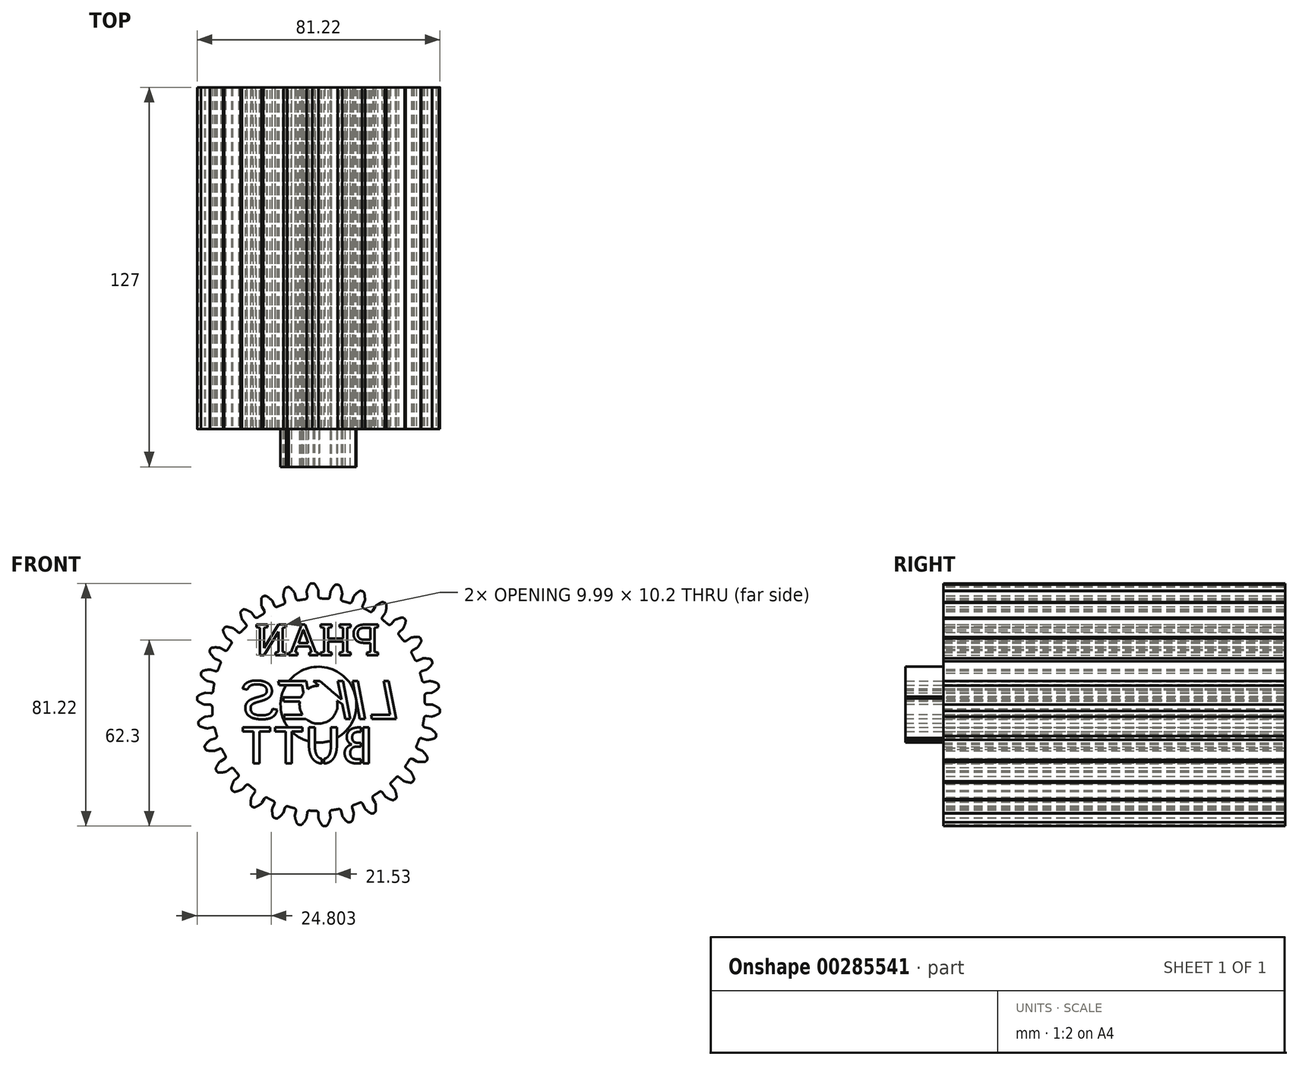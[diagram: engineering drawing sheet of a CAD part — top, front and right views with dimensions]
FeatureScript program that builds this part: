
annotation { "Feature Type Name" : "Feature", "Feature Type Description" : "" }
export const myFeature = defineFeature(function(context is Context, id is Id, definition is map)
    precondition{}
    {
        {
            var Q0;
            Q0=qCreatedBy(makeId("Front.planeOp"),FACE);
            var sketch = newSketch(context, id + "F0", { "sketchPlane" : qUnion([Q0])});
            skCircle(sketch, "E0", {"center": v(0, 0) * mm, "radius": 35.56 * mm});
            skSolve(sketch);
        }
        {
            var Q0;
            Q0=makeQuery(id+"F0.imprint","IMPRINT",FACE,{"disambiguationData":[TD([[makeQuery(id+"F0.imprint","IMPRINT",EDGE,{"derivedFrom":sQuery(id+"F0.wireOp",EDGE,"E0")}),1.0]])]});
            extrude(context, id + "F1", {"entities" : qUnion([Q0]), "depth" : 114.3 * mm});
        }
        {
            var Q0;
            Q0=makeQuery(id+"F1.opExtrude","CAP_FACE",FACE,{"disambiguationData":[OSD([sQuery(id+"F0.wireOp",EDGE,"E0")])],"isStart":false});
            var sketch = newSketch(context, id + "F2", { "sketchPlane" : qUnion([Q0])});
            skArc(sketch, "E1.trimOffspring", {"start": v(-0.06, 38.24) * mm, "mid": v(-0.56, 39.3) * mm, "end": v(-1.2, 40.3) * mm});
            skLineSegment(sketch, "E2", {"start": v(-1.82, 40.61) * mm, "end": v(-2.13, 40.61) * mm});
            skLineSegment(sketch, "E3", {"start": v(0, 37.96) * mm, "end": v(0, 36.31) * mm});
            skLineSegment(sketch, "E4.MirrorCS", {"start": v(-3.97, 37.75) * mm, "end": v(-3.8, 36.12) * mm});
            skArc(sketch, "E5.MirrorCS", {"start": v(-3.94, 38.04) * mm, "mid": v(-3.55, 39.15) * mm, "end": v(-3.02, 40.2) * mm});
            skLineSegment(sketch, "E6.MirrorCS", {"start": v(-2.44, 40.58) * mm, "end": v(-2.13, 40.61) * mm});
            skPoint(sketch, "E7.visualSharp", {"position": v(-3.72, 35.37) * mm});
            skArc(sketch, "E7.filletArc", {"start": v(-4.46, 35.28) * mm, "mid": v(-3.96, 35.56) * mm, "end": v(-3.8, 36.12) * mm});
            skPoint(sketch, "E8.visualSharp", {"position": v(0, 35.56) * mm});
            skArc(sketch, "E8.filletArc", {"start": v(0, 36.31) * mm, "mid": v(0.22, 35.78) * mm, "end": v(0.75, 35.55) * mm});
            skPoint(sketch, "E9.visualSharp", {"position": v(0, 38.1) * mm});
            skArc(sketch, "E9.filletArc", {"start": v(0, 37.96) * mm, "mid": v(-0.01, 38.1) * mm, "end": v(-0.06, 38.24) * mm});
            skPoint(sketch, "E10.visualSharp", {"position": v(-1.44, 40.61) * mm});
            skArc(sketch, "E10.filletArc", {"start": v(-1.2, 40.3) * mm, "mid": v(-1.47, 40.53) * mm, "end": v(-1.82, 40.61) * mm});
            skPoint(sketch, "E11.visualSharp", {"position": v(-3.98, 37.9) * mm});
            skArc(sketch, "E11.filletArc", {"start": v(-3.94, 38.04) * mm, "mid": v(-3.97, 37.9) * mm, "end": v(-3.97, 37.75) * mm});
            skPoint(sketch, "E12.visualSharp", {"position": v(-2.81, 40.54) * mm});
            skArc(sketch, "E12.filletArc", {"start": v(-2.44, 40.58) * mm, "mid": v(-2.77, 40.46) * mm, "end": v(-3.02, 40.2) * mm});
            skArc(sketch, "E13", {"start": v(0.75, 35.55) * mm, "mid": v(-1.86, 35.51) * mm, "end": v(-4.46, 35.28) * mm});
            skPoint(sketch, "E14.1.0", {"position": v(-11.18, 39.07) * mm});
            skPoint(sketch, "E14.1.1", {"position": v(-10.99, 33.82) * mm});
            skPoint(sketch, "E14.1.2", {"position": v(-11.77, 36.24) * mm});
            skArc(sketch, "E14.1.3", {"start": v(-6.66, 34.93) * mm, "mid": v(-9.2, 34.35) * mm, "end": v(-11.7, 33.58) * mm});
            skPoint(sketch, "E14.1.4", {"position": v(-7.92, 37.27) * mm});
            skPoint(sketch, "E14.1.5", {"position": v(-7.4, 34.78) * mm});
            skPoint(sketch, "E14.1.6", {"position": v(-9.85, 39.43) * mm});
            skArc(sketch, "E14.1.7", {"start": v(-11.76, 36.39) * mm, "mid": v(-11.61, 37.56) * mm, "end": v(-11.31, 38.7) * mm});
            skArc(sketch, "E14.1.8", {"start": v(-8, 37.4) * mm, "mid": v(-8.72, 38.33) * mm, "end": v(-9.55, 39.17) * mm});
            skArc(sketch, "E14.1.9", {"start": v(-7.55, 35.52) * mm, "mid": v(-7.23, 35.04) * mm, "end": v(-6.66, 34.93) * mm});
            skArc(sketch, "E14.1.10", {"start": v(-11.76, 36.39) * mm, "mid": v(-11.76, 36.24) * mm, "end": v(-11.73, 36.1) * mm});
            skArc(sketch, "E14.1.11", {"start": v(-9.55, 39.17) * mm, "mid": v(-9.87, 39.34) * mm, "end": v(-10.22, 39.35) * mm});
            skLineSegment(sketch, "E14.1.12", {"start": v(-10.82, 39.19) * mm, "end": v(-10.53, 39.28) * mm});
            skArc(sketch, "E14.1.13", {"start": v(-7.9, 37.13) * mm, "mid": v(-7.94, 37.27) * mm, "end": v(-8, 37.4) * mm});
            skArc(sketch, "E14.1.14", {"start": v(-10.82, 39.19) * mm, "mid": v(-11.13, 39) * mm, "end": v(-11.31, 38.7) * mm});
            skLineSegment(sketch, "E14.1.15", {"start": v(-10.22, 39.35) * mm, "end": v(-10.53, 39.28) * mm});
            skArc(sketch, "E14.1.16", {"start": v(-11.7, 33.58) * mm, "mid": v(-11.26, 33.96) * mm, "end": v(-11.22, 34.54) * mm});
            skLineSegment(sketch, "E14.1.17", {"start": v(-7.9, 37.13) * mm, "end": v(-7.55, 35.52) * mm});
            skLineSegment(sketch, "E14.1.18", {"start": v(-11.73, 36.1) * mm, "end": v(-11.22, 34.54) * mm});
            skPoint(sketch, "E14.2.0", {"position": v(-19.06, 35.9) * mm});
            skPoint(sketch, "E14.2.1", {"position": v(-17.78, 30.8) * mm});
            skPoint(sketch, "E14.2.2", {"position": v(-19.05, 33) * mm});
            skArc(sketch, "E14.2.3", {"start": v(-13.78, 32.78) * mm, "mid": v(-16.14, 31.68) * mm, "end": v(-18.42, 30.42) * mm});
            skPoint(sketch, "E14.2.4", {"position": v(-15.5, 34.8) * mm});
            skPoint(sketch, "E14.2.5", {"position": v(-14.46, 32.49) * mm});
            skPoint(sketch, "E14.2.6", {"position": v(-17.83, 36.52) * mm});
            skArc(sketch, "E14.2.7", {"start": v(-19.07, 33.14) * mm, "mid": v(-19.17, 34.32) * mm, "end": v(-19.11, 35.5) * mm});
            skArc(sketch, "E14.2.8", {"start": v(-15.6, 34.91) * mm, "mid": v(-16.5, 35.68) * mm, "end": v(-17.49, 36.33) * mm});
            skArc(sketch, "E14.2.9", {"start": v(-14.77, 33.17) * mm, "mid": v(-14.35, 32.78) * mm, "end": v(-13.78, 32.78) * mm});
            skArc(sketch, "E14.2.10", {"start": v(-19.07, 33.14) * mm, "mid": v(-19.04, 33) * mm, "end": v(-18.98, 32.87) * mm});
            skArc(sketch, "E14.2.11", {"start": v(-17.49, 36.33) * mm, "mid": v(-17.83, 36.43) * mm, "end": v(-18.18, 36.36) * mm});
            skLineSegment(sketch, "E14.2.12", {"start": v(-18.73, 36.08) * mm, "end": v(-18.46, 36.24) * mm});
            skArc(sketch, "E14.2.13", {"start": v(-15.44, 34.67) * mm, "mid": v(-15.5, 34.8) * mm, "end": v(-15.6, 34.91) * mm});
            skArc(sketch, "E14.2.14", {"start": v(-18.73, 36.08) * mm, "mid": v(-19, 35.84) * mm, "end": v(-19.11, 35.5) * mm});
            skLineSegment(sketch, "E14.2.15", {"start": v(-18.18, 36.36) * mm, "end": v(-18.46, 36.24) * mm});
            skArc(sketch, "E14.2.16", {"start": v(-18.42, 30.42) * mm, "mid": v(-18.08, 30.88) * mm, "end": v(-18.16, 31.45) * mm});
            skLineSegment(sketch, "E14.2.17", {"start": v(-15.44, 34.67) * mm, "end": v(-14.77, 33.17) * mm});
            skLineSegment(sketch, "E14.2.18", {"start": v(-18.98, 32.87) * mm, "end": v(-18.16, 31.45) * mm});
            skPoint(sketch, "E15.1.3.0", {"position": v(-23.8, 26.43) * mm});
            skPoint(sketch, "E15.2.3.0", {"position": v(-25.5, 28.31) * mm});
            skArc(sketch, "E15.3.3.0", {"start": v(-20.3, 29.2) * mm, "mid": v(-22.38, 27.64) * mm, "end": v(-24.34, 25.92) * mm});
            skPoint(sketch, "E15.7.3.0", {"position": v(-22.4, 30.82) * mm});
            skPoint(sketch, "E15.8.3.0", {"position": v(-20.9, 28.77) * mm});
            skPoint(sketch, "E15.9.3.0", {"position": v(-25.04, 32.01) * mm});
            skArc(sketch, "E15.10.3.0", {"start": v(-25.55, 28.45) * mm, "mid": v(-25.88, 29.59) * mm, "end": v(-26.08, 30.75) * mm});
            skArc(sketch, "E15.14.3.0", {"start": v(-22.52, 30.9) * mm, "mid": v(-23.56, 31.47) * mm, "end": v(-24.66, 31.9) * mm});
            skPoint(sketch, "E15.15.3.0", {"position": v(-26.1, 31.15) * mm});
            skArc(sketch, "E15.18.3.0", {"start": v(-21.34, 29.38) * mm, "mid": v(-20.86, 29.08) * mm, "end": v(-20.3, 29.2) * mm});
            skArc(sketch, "E15.22.3.0", {"start": v(-25.55, 28.45) * mm, "mid": v(-25.48, 28.32) * mm, "end": v(-25.4, 28.2) * mm});
            skArc(sketch, "E15.26.3.0", {"start": v(-24.66, 31.9) * mm, "mid": v(-25.01, 31.93) * mm, "end": v(-25.34, 31.8) * mm});
            skLineSegment(sketch, "E15.30.3.0", {"start": v(-25.83, 31.4) * mm, "end": v(-25.6, 31.6) * mm});
            skArc(sketch, "E15.33.3.0", {"start": v(-22.3, 30.7) * mm, "mid": v(-22.4, 30.82) * mm, "end": v(-22.52, 30.9) * mm});
            skArc(sketch, "E15.37.3.0", {"start": v(-25.83, 31.4) * mm, "mid": v(-26.03, 31.1) * mm, "end": v(-26.08, 30.75) * mm});
            skLineSegment(sketch, "E15.41.3.0", {"start": v(-25.34, 31.8) * mm, "end": v(-25.6, 31.6) * mm});
            skArc(sketch, "E15.44.3.0", {"start": v(-24.34, 25.92) * mm, "mid": v(-24.1, 26.44) * mm, "end": v(-24.3, 26.99) * mm});
            skLineSegment(sketch, "E15.48.3.0", {"start": v(-22.3, 30.7) * mm, "end": v(-21.34, 29.38) * mm});
            skLineSegment(sketch, "E15.51.3.0", {"start": v(-25.4, 28.2) * mm, "end": v(-24.3, 26.99) * mm});
            skPoint(sketch, "E15.1.4.0", {"position": v(-28.77, 20.9) * mm});
            skPoint(sketch, "E15.2.4.0", {"position": v(-30.82, 22.4) * mm});
            skArc(sketch, "E15.3.4.0", {"start": v(-25.92, 24.34) * mm, "mid": v(-27.64, 22.38) * mm, "end": v(-29.2, 20.3) * mm});
            skPoint(sketch, "E15.7.4.0", {"position": v(-28.31, 25.5) * mm});
            skPoint(sketch, "E15.8.4.0", {"position": v(-26.43, 23.8) * mm});
            skPoint(sketch, "E15.9.4.0", {"position": v(-31.15, 26.1) * mm});
            skArc(sketch, "E15.10.4.0", {"start": v(-30.9, 22.52) * mm, "mid": v(-31.47, 23.56) * mm, "end": v(-31.9, 24.66) * mm});
            skArc(sketch, "E15.14.4.0", {"start": v(-28.45, 25.55) * mm, "mid": v(-29.59, 25.88) * mm, "end": v(-30.75, 26.08) * mm});
            skPoint(sketch, "E15.15.4.0", {"position": v(-32.01, 25.04) * mm});
            skArc(sketch, "E15.18.4.0", {"start": v(-26.99, 24.3) * mm, "mid": v(-26.44, 24.1) * mm, "end": v(-25.92, 24.34) * mm});
            skArc(sketch, "E15.22.4.0", {"start": v(-30.9, 22.52) * mm, "mid": v(-30.82, 22.4) * mm, "end": v(-30.7, 22.3) * mm});
            skArc(sketch, "E15.26.4.0", {"start": v(-30.75, 26.08) * mm, "mid": v(-31.1, 26.03) * mm, "end": v(-31.4, 25.83) * mm});
            skLineSegment(sketch, "E15.30.4.0", {"start": v(-31.8, 25.34) * mm, "end": v(-31.6, 25.6) * mm});
            skArc(sketch, "E15.33.4.0", {"start": v(-28.2, 25.4) * mm, "mid": v(-28.32, 25.48) * mm, "end": v(-28.45, 25.55) * mm});
            skArc(sketch, "E15.37.4.0", {"start": v(-31.8, 25.34) * mm, "mid": v(-31.93, 25.01) * mm, "end": v(-31.9, 24.66) * mm});
            skLineSegment(sketch, "E15.41.4.0", {"start": v(-31.4, 25.83) * mm, "end": v(-31.6, 25.6) * mm});
            skArc(sketch, "E15.44.4.0", {"start": v(-29.2, 20.3) * mm, "mid": v(-29.08, 20.86) * mm, "end": v(-29.38, 21.34) * mm});
            skLineSegment(sketch, "E15.48.4.0", {"start": v(-28.2, 25.4) * mm, "end": v(-26.99, 24.3) * mm});
            skLineSegment(sketch, "E15.51.4.0", {"start": v(-30.7, 22.3) * mm, "end": v(-29.38, 21.34) * mm});
            skPoint(sketch, "E15.1.5.0", {"position": v(-32.49, 14.46) * mm});
            skPoint(sketch, "E15.2.5.0", {"position": v(-34.8, 15.5) * mm});
            skArc(sketch, "E15.3.5.0", {"start": v(-30.42, 18.42) * mm, "mid": v(-31.68, 16.14) * mm, "end": v(-32.78, 13.78) * mm});
            skPoint(sketch, "E15.7.5.0", {"position": v(-33, 19.05) * mm});
            skPoint(sketch, "E15.8.5.0", {"position": v(-30.8, 17.78) * mm});
            skPoint(sketch, "E15.9.5.0", {"position": v(-35.9, 19.06) * mm});
            skArc(sketch, "E15.10.5.0", {"start": v(-34.91, 15.6) * mm, "mid": v(-35.68, 16.5) * mm, "end": v(-36.33, 17.49) * mm});
            skArc(sketch, "E15.14.5.0", {"start": v(-33.14, 19.07) * mm, "mid": v(-34.32, 19.17) * mm, "end": v(-35.5, 19.11) * mm});
            skPoint(sketch, "E15.15.5.0", {"position": v(-36.52, 17.83) * mm});
            skArc(sketch, "E15.18.5.0", {"start": v(-31.45, 18.16) * mm, "mid": v(-30.88, 18.08) * mm, "end": v(-30.42, 18.42) * mm});
            skArc(sketch, "E15.22.5.0", {"start": v(-34.91, 15.6) * mm, "mid": v(-34.8, 15.5) * mm, "end": v(-34.67, 15.44) * mm});
            skArc(sketch, "E15.26.5.0", {"start": v(-35.5, 19.11) * mm, "mid": v(-35.84, 19) * mm, "end": v(-36.08, 18.73) * mm});
            skLineSegment(sketch, "E15.30.5.0", {"start": v(-36.36, 18.18) * mm, "end": v(-36.24, 18.46) * mm});
            skArc(sketch, "E15.33.5.0", {"start": v(-32.87, 18.98) * mm, "mid": v(-33, 19.04) * mm, "end": v(-33.14, 19.07) * mm});
            skArc(sketch, "E15.37.5.0", {"start": v(-36.36, 18.18) * mm, "mid": v(-36.43, 17.83) * mm, "end": v(-36.33, 17.49) * mm});
            skLineSegment(sketch, "E15.41.5.0", {"start": v(-36.08, 18.73) * mm, "end": v(-36.24, 18.46) * mm});
            skArc(sketch, "E15.44.5.0", {"start": v(-32.78, 13.78) * mm, "mid": v(-32.78, 14.35) * mm, "end": v(-33.17, 14.77) * mm});
            skLineSegment(sketch, "E15.48.5.0", {"start": v(-32.87, 18.98) * mm, "end": v(-31.45, 18.16) * mm});
            skLineSegment(sketch, "E15.51.5.0", {"start": v(-34.67, 15.44) * mm, "end": v(-33.17, 14.77) * mm});
            skPoint(sketch, "E15.1.6.0", {"position": v(-34.78, 7.4) * mm});
            skPoint(sketch, "E15.2.6.0", {"position": v(-37.27, 7.92) * mm});
            skArc(sketch, "E15.3.6.0", {"start": v(-33.58, 11.7) * mm, "mid": v(-34.35, 9.2) * mm, "end": v(-34.93, 6.66) * mm});
            skPoint(sketch, "E15.7.6.0", {"position": v(-36.24, 11.77) * mm});
            skPoint(sketch, "E15.8.6.0", {"position": v(-33.82, 10.99) * mm});
            skPoint(sketch, "E15.9.6.0", {"position": v(-39.07, 11.18) * mm});
            skArc(sketch, "E15.10.6.0", {"start": v(-37.4, 8) * mm, "mid": v(-38.33, 8.72) * mm, "end": v(-39.17, 9.55) * mm});
            skArc(sketch, "E15.14.6.0", {"start": v(-36.39, 11.76) * mm, "mid": v(-37.56, 11.61) * mm, "end": v(-38.7, 11.31) * mm});
            skPoint(sketch, "E15.15.6.0", {"position": v(-39.43, 9.85) * mm});
            skArc(sketch, "E15.18.6.0", {"start": v(-34.54, 11.22) * mm, "mid": v(-33.96, 11.26) * mm, "end": v(-33.58, 11.7) * mm});
            skArc(sketch, "E15.22.6.0", {"start": v(-37.4, 8) * mm, "mid": v(-37.27, 7.94) * mm, "end": v(-37.13, 7.9) * mm});
            skArc(sketch, "E15.26.6.0", {"start": v(-38.7, 11.31) * mm, "mid": v(-39, 11.13) * mm, "end": v(-39.19, 10.82) * mm});
            skLineSegment(sketch, "E15.30.6.0", {"start": v(-39.35, 10.22) * mm, "end": v(-39.28, 10.53) * mm});
            skArc(sketch, "E15.33.6.0", {"start": v(-36.1, 11.73) * mm, "mid": v(-36.24, 11.76) * mm, "end": v(-36.39, 11.76) * mm});
            skArc(sketch, "E15.37.6.0", {"start": v(-39.35, 10.22) * mm, "mid": v(-39.34, 9.87) * mm, "end": v(-39.17, 9.55) * mm});
            skLineSegment(sketch, "E15.41.6.0", {"start": v(-39.19, 10.82) * mm, "end": v(-39.28, 10.53) * mm});
            skArc(sketch, "E15.44.6.0", {"start": v(-34.93, 6.66) * mm, "mid": v(-35.04, 7.23) * mm, "end": v(-35.52, 7.55) * mm});
            skLineSegment(sketch, "E15.48.6.0", {"start": v(-36.1, 11.73) * mm, "end": v(-34.54, 11.22) * mm});
            skLineSegment(sketch, "E15.51.6.0", {"start": v(-37.13, 7.9) * mm, "end": v(-35.52, 7.55) * mm});
            skPoint(sketch, "E15.1.7.0", {"position": v(-35.56, 0) * mm});
            skPoint(sketch, "E15.2.7.0", {"position": v(-38.1, 0) * mm});
            skArc(sketch, "E15.3.7.0", {"start": v(-35.28, 4.46) * mm, "mid": v(-35.51, 1.86) * mm, "end": v(-35.55, -0.75) * mm});
            skPoint(sketch, "E15.7.7.0", {"position": v(-37.9, 3.98) * mm});
            skPoint(sketch, "E15.8.7.0", {"position": v(-35.37, 3.72) * mm});
            skPoint(sketch, "E15.9.7.0", {"position": v(-40.54, 2.81) * mm});
            skArc(sketch, "E15.10.7.0", {"start": v(-38.24, 0.06) * mm, "mid": v(-39.3, 0.56) * mm, "end": v(-40.3, 1.2) * mm});
            skArc(sketch, "E15.14.7.0", {"start": v(-38.04, 3.94) * mm, "mid": v(-39.15, 3.55) * mm, "end": v(-40.2, 3.02) * mm});
            skPoint(sketch, "E15.15.7.0", {"position": v(-40.61, 1.44) * mm});
            skArc(sketch, "E15.18.7.0", {"start": v(-36.12, 3.8) * mm, "mid": v(-35.56, 3.96) * mm, "end": v(-35.28, 4.46) * mm});
            skArc(sketch, "E15.22.7.0", {"start": v(-38.24, 0.06) * mm, "mid": v(-38.1, 0.01) * mm, "end": v(-37.96, 0) * mm});
            skArc(sketch, "E15.26.7.0", {"start": v(-40.2, 3.02) * mm, "mid": v(-40.46, 2.77) * mm, "end": v(-40.58, 2.44) * mm});
            skLineSegment(sketch, "E15.30.7.0", {"start": v(-40.61, 1.82) * mm, "end": v(-40.61, 2.13) * mm});
            skArc(sketch, "E15.33.7.0", {"start": v(-37.75, 3.97) * mm, "mid": v(-37.9, 3.97) * mm, "end": v(-38.04, 3.94) * mm});
            skArc(sketch, "E15.37.7.0", {"start": v(-40.61, 1.82) * mm, "mid": v(-40.53, 1.47) * mm, "end": v(-40.3, 1.2) * mm});
            skLineSegment(sketch, "E15.41.7.0", {"start": v(-40.58, 2.44) * mm, "end": v(-40.61, 2.13) * mm});
            skArc(sketch, "E15.44.7.0", {"start": v(-35.55, -0.75) * mm, "mid": v(-35.78, -0.22) * mm, "end": v(-36.31, 0) * mm});
            skLineSegment(sketch, "E15.48.7.0", {"start": v(-37.75, 3.97) * mm, "end": v(-36.12, 3.8) * mm});
            skLineSegment(sketch, "E15.51.7.0", {"start": v(-37.96, 0) * mm, "end": v(-36.31, 0) * mm});
            skPoint(sketch, "E15.1.8.0", {"position": v(-34.78, -7.4) * mm});
            skPoint(sketch, "E15.2.8.0", {"position": v(-37.27, -7.92) * mm});
            skArc(sketch, "E15.3.8.0", {"start": v(-35.44, -2.97) * mm, "mid": v(-35.12, -5.56) * mm, "end": v(-34.62, -8.12) * mm});
            skPoint(sketch, "E15.7.8.0", {"position": v(-37.9, -3.98) * mm});
            skPoint(sketch, "E15.8.8.0", {"position": v(-35.37, -3.72) * mm});
            skPoint(sketch, "E15.9.8.0", {"position": v(-40.24, -5.68) * mm});
            skArc(sketch, "E15.10.8.0", {"start": v(-37.42, -7.9) * mm, "mid": v(-38.57, -7.62) * mm, "end": v(-39.67, -7.2) * mm});
            skArc(sketch, "E15.14.8.0", {"start": v(-38.02, -4.05) * mm, "mid": v(-39.03, -4.67) * mm, "end": v(-39.96, -5.4) * mm});
            skPoint(sketch, "E15.15.8.0", {"position": v(-40.03, -7.04) * mm});
            skArc(sketch, "E15.18.8.0", {"start": v(-36.12, -3.8) * mm, "mid": v(-35.6, -3.52) * mm, "end": v(-35.44, -2.97) * mm});
            skArc(sketch, "E15.22.8.0", {"start": v(-37.42, -7.9) * mm, "mid": v(-37.27, -7.9) * mm, "end": v(-37.13, -7.9) * mm});
            skArc(sketch, "E15.26.8.0", {"start": v(-39.96, -5.4) * mm, "mid": v(-40.16, -5.7) * mm, "end": v(-40.2, -6.05) * mm});
            skLineSegment(sketch, "E15.30.8.0", {"start": v(-40.1, -6.67) * mm, "end": v(-40.17, -6.36) * mm});
            skArc(sketch, "E15.33.8.0", {"start": v(-37.75, -3.97) * mm, "mid": v(-37.9, -4) * mm, "end": v(-38.02, -4.05) * mm});
            skArc(sketch, "E15.37.8.0", {"start": v(-40.1, -6.67) * mm, "mid": v(-39.95, -6.99) * mm, "end": v(-39.67, -7.2) * mm});
            skLineSegment(sketch, "E15.41.8.0", {"start": v(-40.2, -6.05) * mm, "end": v(-40.17, -6.36) * mm});
            skArc(sketch, "E15.44.8.0", {"start": v(-34.62, -8.12) * mm, "mid": v(-34.95, -7.65) * mm, "end": v(-35.52, -7.55) * mm});
            skLineSegment(sketch, "E15.48.8.0", {"start": v(-37.75, -3.97) * mm, "end": v(-36.12, -3.8) * mm});
            skLineSegment(sketch, "E15.51.8.0", {"start": v(-37.13, -7.9) * mm, "end": v(-35.52, -7.55) * mm});
            skPoint(sketch, "E15.1.9.0", {"position": v(-32.49, -14.46) * mm});
            skPoint(sketch, "E15.2.9.0", {"position": v(-34.8, -15.5) * mm});
            skArc(sketch, "E15.3.9.0", {"start": v(-34.04, -10.28) * mm, "mid": v(-33.2, -12.74) * mm, "end": v(-32.18, -15.14) * mm});
            skPoint(sketch, "E15.7.9.0", {"position": v(-36.24, -11.77) * mm});
            skPoint(sketch, "E15.8.9.0", {"position": v(-33.82, -10.99) * mm});
            skPoint(sketch, "E15.9.9.0", {"position": v(-38.18, -13.92) * mm});
            skArc(sketch, "E15.10.9.0", {"start": v(-34.96, -15.5) * mm, "mid": v(-36.14, -15.47) * mm, "end": v(-37.3, -15.3) * mm});
            skArc(sketch, "E15.14.9.0", {"start": v(-36.35, -11.87) * mm, "mid": v(-37.2, -12.68) * mm, "end": v(-37.96, -13.6) * mm});
            skPoint(sketch, "E15.15.9.0", {"position": v(-37.69, -15.2) * mm});
            skArc(sketch, "E15.18.9.0", {"start": v(-34.54, -11.22) * mm, "mid": v(-34.1, -10.85) * mm, "end": v(-34.04, -10.28) * mm});
            skArc(sketch, "E15.22.9.0", {"start": v(-34.96, -15.5) * mm, "mid": v(-34.81, -15.48) * mm, "end": v(-34.67, -15.44) * mm});
            skArc(sketch, "E15.26.9.0", {"start": v(-37.96, -13.6) * mm, "mid": v(-38.1, -13.92) * mm, "end": v(-38.07, -14.28) * mm});
            skLineSegment(sketch, "E15.30.9.0", {"start": v(-37.84, -14.86) * mm, "end": v(-37.97, -14.57) * mm});
            skArc(sketch, "E15.33.9.0", {"start": v(-36.1, -11.73) * mm, "mid": v(-36.23, -11.79) * mm, "end": v(-36.35, -11.87) * mm});
            skArc(sketch, "E15.37.9.0", {"start": v(-37.84, -14.86) * mm, "mid": v(-37.63, -15.14) * mm, "end": v(-37.3, -15.3) * mm});
            skLineSegment(sketch, "E15.41.9.0", {"start": v(-38.07, -14.28) * mm, "end": v(-37.97, -14.57) * mm});
            skArc(sketch, "E15.44.9.0", {"start": v(-32.18, -15.14) * mm, "mid": v(-32.6, -14.75) * mm, "end": v(-33.17, -14.77) * mm});
            skLineSegment(sketch, "E15.48.9.0", {"start": v(-36.1, -11.73) * mm, "end": v(-34.54, -11.22) * mm});
            skLineSegment(sketch, "E15.51.9.0", {"start": v(-34.67, -15.44) * mm, "end": v(-33.17, -14.77) * mm});
            skPoint(sketch, "E15.1.10.0", {"position": v(-28.77, -20.9) * mm});
            skPoint(sketch, "E15.2.10.0", {"position": v(-30.82, -22.4) * mm});
            skArc(sketch, "E15.3.10.0", {"start": v(-31.16, -17.13) * mm, "mid": v(-29.82, -19.37) * mm, "end": v(-28.32, -21.5) * mm});
            skPoint(sketch, "E15.7.10.0", {"position": v(-33, -19.05) * mm});
            skPoint(sketch, "E15.8.10.0", {"position": v(-30.8, -17.78) * mm});
            skPoint(sketch, "E15.9.10.0", {"position": v(-34.45, -21.55) * mm});
            skArc(sketch, "E15.10.10.0", {"start": v(-30.97, -22.43) * mm, "mid": v(-32.13, -22.65) * mm, "end": v(-33.31, -22.72) * mm});
            skArc(sketch, "E15.14.10.0", {"start": v(-33.09, -19.17) * mm, "mid": v(-33.76, -20.14) * mm, "end": v(-34.3, -21.2) * mm});
            skPoint(sketch, "E15.15.10.0", {"position": v(-33.7, -22.7) * mm});
            skArc(sketch, "E15.18.10.0", {"start": v(-31.45, -18.16) * mm, "mid": v(-31.1, -17.7) * mm, "end": v(-31.16, -17.13) * mm});
            skArc(sketch, "E15.22.10.0", {"start": v(-30.97, -22.43) * mm, "mid": v(-30.83, -22.38) * mm, "end": v(-30.7, -22.3) * mm});
            skArc(sketch, "E15.26.10.0", {"start": v(-34.3, -21.2) * mm, "mid": v(-34.37, -21.54) * mm, "end": v(-34.27, -21.88) * mm});
            skLineSegment(sketch, "E15.30.10.0", {"start": v(-33.93, -22.4) * mm, "end": v(-34.1, -22.15) * mm});
            skArc(sketch, "E15.33.10.0", {"start": v(-32.87, -18.98) * mm, "mid": v(-32.99, -19.06) * mm, "end": v(-33.09, -19.17) * mm});
            skArc(sketch, "E15.37.10.0", {"start": v(-33.93, -22.4) * mm, "mid": v(-33.66, -22.63) * mm, "end": v(-33.31, -22.72) * mm});
            skLineSegment(sketch, "E15.41.10.0", {"start": v(-34.27, -21.88) * mm, "end": v(-34.1, -22.15) * mm});
            skArc(sketch, "E15.44.10.0", {"start": v(-28.32, -21.5) * mm, "mid": v(-28.82, -21.2) * mm, "end": v(-29.38, -21.34) * mm});
            skLineSegment(sketch, "E15.48.10.0", {"start": v(-32.87, -18.98) * mm, "end": v(-31.45, -18.16) * mm});
            skLineSegment(sketch, "E15.51.10.0", {"start": v(-30.7, -22.3) * mm, "end": v(-29.38, -21.34) * mm});
            skPoint(sketch, "E15.1.11.0", {"position": v(-23.8, -26.43) * mm});
            skPoint(sketch, "E15.2.11.0", {"position": v(-25.5, -28.31) * mm});
            skArc(sketch, "E15.3.11.0", {"start": v(-26.92, -23.23) * mm, "mid": v(-25.14, -25.14) * mm, "end": v(-23.23, -26.92) * mm});
            skPoint(sketch, "E15.7.11.0", {"position": v(-28.31, -25.5) * mm});
            skPoint(sketch, "E15.8.11.0", {"position": v(-26.43, -23.8) * mm});
            skPoint(sketch, "E15.9.11.0", {"position": v(-29.22, -28.25) * mm});
            skArc(sketch, "E15.10.11.0", {"start": v(-25.63, -28.38) * mm, "mid": v(-26.72, -28.83) * mm, "end": v(-27.86, -29.15) * mm});
            skArc(sketch, "E15.14.11.0", {"start": v(-28.38, -25.63) * mm, "mid": v(-28.83, -26.72) * mm, "end": v(-29.15, -27.86) * mm});
            skPoint(sketch, "E15.15.11.0", {"position": v(-28.25, -29.22) * mm});
            skArc(sketch, "E15.18.11.0", {"start": v(-26.99, -24.3) * mm, "mid": v(-26.74, -23.78) * mm, "end": v(-26.92, -23.23) * mm});
            skArc(sketch, "E15.22.11.0", {"start": v(-25.63, -28.38) * mm, "mid": v(-25.5, -28.3) * mm, "end": v(-25.4, -28.2) * mm});
            skArc(sketch, "E15.26.11.0", {"start": v(-29.15, -27.86) * mm, "mid": v(-29.14, -28.21) * mm, "end": v(-28.97, -28.53) * mm});
            skLineSegment(sketch, "E15.30.11.0", {"start": v(-28.53, -28.97) * mm, "end": v(-28.76, -28.76) * mm});
            skArc(sketch, "E15.33.11.0", {"start": v(-28.2, -25.4) * mm, "mid": v(-28.3, -25.5) * mm, "end": v(-28.38, -25.63) * mm});
            skArc(sketch, "E15.37.11.0", {"start": v(-28.53, -28.97) * mm, "mid": v(-28.21, -29.14) * mm, "end": v(-27.86, -29.15) * mm});
            skLineSegment(sketch, "E15.41.11.0", {"start": v(-28.97, -28.53) * mm, "end": v(-28.76, -28.76) * mm});
            skArc(sketch, "E15.44.11.0", {"start": v(-23.23, -26.92) * mm, "mid": v(-23.78, -26.74) * mm, "end": v(-24.3, -26.99) * mm});
            skLineSegment(sketch, "E15.48.11.0", {"start": v(-28.2, -25.4) * mm, "end": v(-26.99, -24.3) * mm});
            skLineSegment(sketch, "E15.51.11.0", {"start": v(-25.4, -28.2) * mm, "end": v(-24.3, -26.99) * mm});
            skPoint(sketch, "E15.1.12.0", {"position": v(-17.78, -30.8) * mm});
            skPoint(sketch, "E15.2.12.0", {"position": v(-19.05, -33) * mm});
            skArc(sketch, "E15.3.12.0", {"start": v(-21.5, -28.32) * mm, "mid": v(-19.37, -29.82) * mm, "end": v(-17.13, -31.16) * mm});
            skPoint(sketch, "E15.7.12.0", {"position": v(-22.4, -30.82) * mm});
            skPoint(sketch, "E15.8.12.0", {"position": v(-20.9, -28.77) * mm});
            skPoint(sketch, "E15.9.12.0", {"position": v(-22.7, -33.7) * mm});
            skArc(sketch, "E15.10.12.0", {"start": v(-19.17, -33.09) * mm, "mid": v(-20.14, -33.76) * mm, "end": v(-21.2, -34.3) * mm});
            skArc(sketch, "E15.14.12.0", {"start": v(-22.43, -30.97) * mm, "mid": v(-22.65, -32.13) * mm, "end": v(-22.72, -33.31) * mm});
            skPoint(sketch, "E15.15.12.0", {"position": v(-21.55, -34.45) * mm});
            skArc(sketch, "E15.18.12.0", {"start": v(-21.34, -29.38) * mm, "mid": v(-21.2, -28.82) * mm, "end": v(-21.5, -28.32) * mm});
            skArc(sketch, "E15.22.12.0", {"start": v(-19.17, -33.09) * mm, "mid": v(-19.06, -32.99) * mm, "end": v(-18.98, -32.87) * mm});
            skArc(sketch, "E15.26.12.0", {"start": v(-22.72, -33.31) * mm, "mid": v(-22.63, -33.66) * mm, "end": v(-22.4, -33.93) * mm});
            skLineSegment(sketch, "E15.30.12.0", {"start": v(-21.88, -34.27) * mm, "end": v(-22.15, -34.1) * mm});
            skArc(sketch, "E15.33.12.0", {"start": v(-22.3, -30.7) * mm, "mid": v(-22.38, -30.83) * mm, "end": v(-22.43, -30.97) * mm});
            skArc(sketch, "E15.37.12.0", {"start": v(-21.88, -34.27) * mm, "mid": v(-21.54, -34.37) * mm, "end": v(-21.2, -34.3) * mm});
            skLineSegment(sketch, "E15.41.12.0", {"start": v(-22.4, -33.93) * mm, "end": v(-22.15, -34.1) * mm});
            skArc(sketch, "E15.44.12.0", {"start": v(-17.13, -31.16) * mm, "mid": v(-17.7, -31.1) * mm, "end": v(-18.16, -31.45) * mm});
            skLineSegment(sketch, "E15.48.12.0", {"start": v(-22.3, -30.7) * mm, "end": v(-21.34, -29.38) * mm});
            skLineSegment(sketch, "E15.51.12.0", {"start": v(-18.98, -32.87) * mm, "end": v(-18.16, -31.45) * mm});
            skPoint(sketch, "E15.1.13.0", {"position": v(-10.99, -33.82) * mm});
            skPoint(sketch, "E15.2.13.0", {"position": v(-11.77, -36.24) * mm});
            skArc(sketch, "E15.3.13.0", {"start": v(-15.14, -32.18) * mm, "mid": v(-12.74, -33.2) * mm, "end": v(-10.28, -34.04) * mm});
            skPoint(sketch, "E15.7.13.0", {"position": v(-15.5, -34.8) * mm});
            skPoint(sketch, "E15.8.13.0", {"position": v(-14.46, -32.49) * mm});
            skPoint(sketch, "E15.9.13.0", {"position": v(-15.2, -37.69) * mm});
            skArc(sketch, "E15.10.13.0", {"start": v(-11.87, -36.35) * mm, "mid": v(-12.68, -37.2) * mm, "end": v(-13.6, -37.96) * mm});
            skArc(sketch, "E15.14.13.0", {"start": v(-15.5, -34.96) * mm, "mid": v(-15.47, -36.14) * mm, "end": v(-15.3, -37.3) * mm});
            skPoint(sketch, "E15.15.13.0", {"position": v(-13.92, -38.18) * mm});
            skArc(sketch, "E15.18.13.0", {"start": v(-14.77, -33.17) * mm, "mid": v(-14.75, -32.6) * mm, "end": v(-15.14, -32.18) * mm});
            skArc(sketch, "E15.22.13.0", {"start": v(-11.87, -36.35) * mm, "mid": v(-11.79, -36.23) * mm, "end": v(-11.73, -36.1) * mm});
            skArc(sketch, "E15.26.13.0", {"start": v(-15.3, -37.3) * mm, "mid": v(-15.14, -37.63) * mm, "end": v(-14.86, -37.84) * mm});
            skLineSegment(sketch, "E15.30.13.0", {"start": v(-14.28, -38.07) * mm, "end": v(-14.57, -37.97) * mm});
            skArc(sketch, "E15.33.13.0", {"start": v(-15.44, -34.67) * mm, "mid": v(-15.48, -34.81) * mm, "end": v(-15.5, -34.96) * mm});
            skArc(sketch, "E15.37.13.0", {"start": v(-14.28, -38.07) * mm, "mid": v(-13.92, -38.1) * mm, "end": v(-13.6, -37.96) * mm});
            skLineSegment(sketch, "E15.41.13.0", {"start": v(-14.86, -37.84) * mm, "end": v(-14.57, -37.97) * mm});
            skArc(sketch, "E15.44.13.0", {"start": v(-10.28, -34.04) * mm, "mid": v(-10.85, -34.1) * mm, "end": v(-11.22, -34.54) * mm});
            skLineSegment(sketch, "E15.48.13.0", {"start": v(-15.44, -34.67) * mm, "end": v(-14.77, -33.17) * mm});
            skLineSegment(sketch, "E15.51.13.0", {"start": v(-11.73, -36.1) * mm, "end": v(-11.22, -34.54) * mm});
            skPoint(sketch, "E15.1.14.0", {"position": v(-3.72, -35.37) * mm});
            skPoint(sketch, "E15.2.14.0", {"position": v(-3.98, -37.9) * mm});
            skArc(sketch, "E15.3.14.0", {"start": v(-8.12, -34.62) * mm, "mid": v(-5.56, -35.12) * mm, "end": v(-2.97, -35.44) * mm});
            skPoint(sketch, "E15.7.14.0", {"position": v(-7.92, -37.27) * mm});
            skPoint(sketch, "E15.8.14.0", {"position": v(-7.4, -34.78) * mm});
            skPoint(sketch, "E15.9.14.0", {"position": v(-7.04, -40.03) * mm});
            skArc(sketch, "E15.10.14.0", {"start": v(-4.05, -38.02) * mm, "mid": v(-4.67, -39.03) * mm, "end": v(-5.4, -39.96) * mm});
            skArc(sketch, "E15.14.14.0", {"start": v(-7.9, -37.42) * mm, "mid": v(-7.62, -38.57) * mm, "end": v(-7.2, -39.67) * mm});
            skPoint(sketch, "E15.15.14.0", {"position": v(-5.68, -40.24) * mm});
            skArc(sketch, "E15.18.14.0", {"start": v(-7.55, -35.52) * mm, "mid": v(-7.65, -34.95) * mm, "end": v(-8.12, -34.62) * mm});
            skArc(sketch, "E15.22.14.0", {"start": v(-4.05, -38.02) * mm, "mid": v(-4, -37.9) * mm, "end": v(-3.97, -37.75) * mm});
            skArc(sketch, "E15.26.14.0", {"start": v(-7.2, -39.67) * mm, "mid": v(-6.99, -39.95) * mm, "end": v(-6.67, -40.1) * mm});
            skLineSegment(sketch, "E15.30.14.0", {"start": v(-6.05, -40.2) * mm, "end": v(-6.36, -40.17) * mm});
            skArc(sketch, "E15.33.14.0", {"start": v(-7.9, -37.13) * mm, "mid": v(-7.9, -37.27) * mm, "end": v(-7.9, -37.42) * mm});
            skArc(sketch, "E15.37.14.0", {"start": v(-6.05, -40.2) * mm, "mid": v(-5.7, -40.16) * mm, "end": v(-5.4, -39.96) * mm});
            skLineSegment(sketch, "E15.41.14.0", {"start": v(-6.67, -40.1) * mm, "end": v(-6.36, -40.17) * mm});
            skArc(sketch, "E15.44.14.0", {"start": v(-2.97, -35.44) * mm, "mid": v(-3.52, -35.6) * mm, "end": v(-3.8, -36.12) * mm});
            skLineSegment(sketch, "E15.48.14.0", {"start": v(-7.9, -37.13) * mm, "end": v(-7.55, -35.52) * mm});
            skLineSegment(sketch, "E15.51.14.0", {"start": v(-3.97, -37.75) * mm, "end": v(-3.8, -36.12) * mm});
            skPoint(sketch, "E15.1.15.0", {"position": v(3.72, -35.37) * mm});
            skPoint(sketch, "E15.2.15.0", {"position": v(3.98, -37.9) * mm});
            skArc(sketch, "E15.3.15.0", {"start": v(-0.75, -35.55) * mm, "mid": v(1.86, -35.51) * mm, "end": v(4.46, -35.28) * mm});
            skPoint(sketch, "E15.7.15.0", {"position": v(0, -38.1) * mm});
            skPoint(sketch, "E15.8.15.0", {"position": v(0, -35.56) * mm});
            skPoint(sketch, "E15.9.15.0", {"position": v(1.44, -40.61) * mm});
            skArc(sketch, "E15.10.15.0", {"start": v(3.94, -38.04) * mm, "mid": v(3.55, -39.15) * mm, "end": v(3.02, -40.2) * mm});
            skArc(sketch, "E15.14.15.0", {"start": v(0.06, -38.24) * mm, "mid": v(0.56, -39.3) * mm, "end": v(1.2, -40.3) * mm});
            skPoint(sketch, "E15.15.15.0", {"position": v(2.81, -40.54) * mm});
            skArc(sketch, "E15.18.15.0", {"start": v(0, -36.31) * mm, "mid": v(-0.22, -35.78) * mm, "end": v(-0.75, -35.55) * mm});
            skArc(sketch, "E15.22.15.0", {"start": v(3.94, -38.04) * mm, "mid": v(3.97, -37.9) * mm, "end": v(3.97, -37.75) * mm});
            skArc(sketch, "E15.26.15.0", {"start": v(1.2, -40.3) * mm, "mid": v(1.47, -40.53) * mm, "end": v(1.82, -40.61) * mm});
            skLineSegment(sketch, "E15.30.15.0", {"start": v(2.44, -40.58) * mm, "end": v(2.13, -40.61) * mm});
            skArc(sketch, "E15.33.15.0", {"start": v(0, -37.96) * mm, "mid": v(0.01, -38.1) * mm, "end": v(0.06, -38.24) * mm});
            skArc(sketch, "E15.37.15.0", {"start": v(2.44, -40.58) * mm, "mid": v(2.77, -40.46) * mm, "end": v(3.02, -40.2) * mm});
            skLineSegment(sketch, "E15.41.15.0", {"start": v(1.82, -40.61) * mm, "end": v(2.13, -40.61) * mm});
            skArc(sketch, "E15.44.15.0", {"start": v(4.46, -35.28) * mm, "mid": v(3.96, -35.56) * mm, "end": v(3.8, -36.12) * mm});
            skLineSegment(sketch, "E15.48.15.0", {"start": v(0, -37.96) * mm, "end": v(0, -36.31) * mm});
            skLineSegment(sketch, "E15.51.15.0", {"start": v(3.97, -37.75) * mm, "end": v(3.8, -36.12) * mm});
            skPoint(sketch, "E15.1.16.0", {"position": v(10.99, -33.82) * mm});
            skPoint(sketch, "E15.2.16.0", {"position": v(11.77, -36.24) * mm});
            skArc(sketch, "E15.3.16.0", {"start": v(6.66, -34.93) * mm, "mid": v(9.2, -34.35) * mm, "end": v(11.7, -33.58) * mm});
            skPoint(sketch, "E15.7.16.0", {"position": v(7.92, -37.27) * mm});
            skPoint(sketch, "E15.8.16.0", {"position": v(7.4, -34.78) * mm});
            skPoint(sketch, "E15.9.16.0", {"position": v(9.85, -39.43) * mm});
            skArc(sketch, "E15.10.16.0", {"start": v(11.76, -36.39) * mm, "mid": v(11.61, -37.56) * mm, "end": v(11.31, -38.7) * mm});
            skArc(sketch, "E15.14.16.0", {"start": v(8, -37.4) * mm, "mid": v(8.72, -38.33) * mm, "end": v(9.55, -39.17) * mm});
            skPoint(sketch, "E15.15.16.0", {"position": v(11.18, -39.07) * mm});
            skArc(sketch, "E15.18.16.0", {"start": v(7.55, -35.52) * mm, "mid": v(7.23, -35.04) * mm, "end": v(6.66, -34.93) * mm});
            skArc(sketch, "E15.22.16.0", {"start": v(11.76, -36.39) * mm, "mid": v(11.76, -36.24) * mm, "end": v(11.73, -36.1) * mm});
            skArc(sketch, "E15.26.16.0", {"start": v(9.55, -39.17) * mm, "mid": v(9.87, -39.34) * mm, "end": v(10.22, -39.35) * mm});
            skLineSegment(sketch, "E15.30.16.0", {"start": v(10.82, -39.19) * mm, "end": v(10.53, -39.28) * mm});
            skArc(sketch, "E15.33.16.0", {"start": v(7.9, -37.13) * mm, "mid": v(7.94, -37.27) * mm, "end": v(8, -37.4) * mm});
            skArc(sketch, "E15.37.16.0", {"start": v(10.82, -39.19) * mm, "mid": v(11.13, -39) * mm, "end": v(11.31, -38.7) * mm});
            skLineSegment(sketch, "E15.41.16.0", {"start": v(10.22, -39.35) * mm, "end": v(10.53, -39.28) * mm});
            skArc(sketch, "E15.44.16.0", {"start": v(11.7, -33.58) * mm, "mid": v(11.26, -33.96) * mm, "end": v(11.22, -34.54) * mm});
            skLineSegment(sketch, "E15.48.16.0", {"start": v(7.9, -37.13) * mm, "end": v(7.55, -35.52) * mm});
            skLineSegment(sketch, "E15.51.16.0", {"start": v(11.73, -36.1) * mm, "end": v(11.22, -34.54) * mm});
            skPoint(sketch, "E15.1.17.0", {"position": v(17.78, -30.8) * mm});
            skPoint(sketch, "E15.2.17.0", {"position": v(19.05, -33) * mm});
            skArc(sketch, "E15.3.17.0", {"start": v(13.78, -32.78) * mm, "mid": v(16.14, -31.68) * mm, "end": v(18.42, -30.42) * mm});
            skPoint(sketch, "E15.7.17.0", {"position": v(15.5, -34.8) * mm});
            skPoint(sketch, "E15.8.17.0", {"position": v(14.46, -32.49) * mm});
            skPoint(sketch, "E15.9.17.0", {"position": v(17.83, -36.52) * mm});
            skArc(sketch, "E15.10.17.0", {"start": v(19.07, -33.14) * mm, "mid": v(19.17, -34.32) * mm, "end": v(19.11, -35.5) * mm});
            skArc(sketch, "E15.14.17.0", {"start": v(15.6, -34.91) * mm, "mid": v(16.5, -35.68) * mm, "end": v(17.49, -36.33) * mm});
            skPoint(sketch, "E15.15.17.0", {"position": v(19.06, -35.9) * mm});
            skArc(sketch, "E15.18.17.0", {"start": v(14.77, -33.17) * mm, "mid": v(14.35, -32.78) * mm, "end": v(13.78, -32.78) * mm});
            skArc(sketch, "E15.22.17.0", {"start": v(19.07, -33.14) * mm, "mid": v(19.04, -33) * mm, "end": v(18.98, -32.87) * mm});
            skArc(sketch, "E15.26.17.0", {"start": v(17.49, -36.33) * mm, "mid": v(17.83, -36.43) * mm, "end": v(18.18, -36.36) * mm});
            skLineSegment(sketch, "E15.30.17.0", {"start": v(18.73, -36.08) * mm, "end": v(18.46, -36.24) * mm});
            skArc(sketch, "E15.33.17.0", {"start": v(15.44, -34.67) * mm, "mid": v(15.5, -34.8) * mm, "end": v(15.6, -34.91) * mm});
            skArc(sketch, "E15.37.17.0", {"start": v(18.73, -36.08) * mm, "mid": v(19, -35.84) * mm, "end": v(19.11, -35.5) * mm});
            skLineSegment(sketch, "E15.41.17.0", {"start": v(18.18, -36.36) * mm, "end": v(18.46, -36.24) * mm});
            skArc(sketch, "E15.44.17.0", {"start": v(18.42, -30.42) * mm, "mid": v(18.08, -30.88) * mm, "end": v(18.16, -31.45) * mm});
            skLineSegment(sketch, "E15.48.17.0", {"start": v(15.44, -34.67) * mm, "end": v(14.77, -33.17) * mm});
            skLineSegment(sketch, "E15.51.17.0", {"start": v(18.98, -32.87) * mm, "end": v(18.16, -31.45) * mm});
            skPoint(sketch, "E15.1.18.0", {"position": v(23.8, -26.43) * mm});
            skPoint(sketch, "E15.2.18.0", {"position": v(25.5, -28.31) * mm});
            skArc(sketch, "E15.3.18.0", {"start": v(20.3, -29.2) * mm, "mid": v(22.38, -27.64) * mm, "end": v(24.34, -25.92) * mm});
            skPoint(sketch, "E15.7.18.0", {"position": v(22.4, -30.82) * mm});
            skPoint(sketch, "E15.8.18.0", {"position": v(20.9, -28.77) * mm});
            skPoint(sketch, "E15.9.18.0", {"position": v(25.04, -32.01) * mm});
            skArc(sketch, "E15.10.18.0", {"start": v(25.55, -28.45) * mm, "mid": v(25.88, -29.59) * mm, "end": v(26.08, -30.75) * mm});
            skArc(sketch, "E15.14.18.0", {"start": v(22.52, -30.9) * mm, "mid": v(23.56, -31.47) * mm, "end": v(24.66, -31.9) * mm});
            skPoint(sketch, "E15.15.18.0", {"position": v(26.1, -31.15) * mm});
            skArc(sketch, "E15.18.18.0", {"start": v(21.34, -29.38) * mm, "mid": v(20.86, -29.08) * mm, "end": v(20.3, -29.2) * mm});
            skArc(sketch, "E15.22.18.0", {"start": v(25.55, -28.45) * mm, "mid": v(25.48, -28.32) * mm, "end": v(25.4, -28.2) * mm});
            skArc(sketch, "E15.26.18.0", {"start": v(24.66, -31.9) * mm, "mid": v(25.01, -31.93) * mm, "end": v(25.34, -31.8) * mm});
            skLineSegment(sketch, "E15.30.18.0", {"start": v(25.83, -31.4) * mm, "end": v(25.6, -31.6) * mm});
            skArc(sketch, "E15.33.18.0", {"start": v(22.3, -30.7) * mm, "mid": v(22.4, -30.82) * mm, "end": v(22.52, -30.9) * mm});
            skArc(sketch, "E15.37.18.0", {"start": v(25.83, -31.4) * mm, "mid": v(26.03, -31.1) * mm, "end": v(26.08, -30.75) * mm});
            skLineSegment(sketch, "E15.41.18.0", {"start": v(25.34, -31.8) * mm, "end": v(25.6, -31.6) * mm});
            skArc(sketch, "E15.44.18.0", {"start": v(24.34, -25.92) * mm, "mid": v(24.1, -26.44) * mm, "end": v(24.3, -26.99) * mm});
            skLineSegment(sketch, "E15.48.18.0", {"start": v(22.3, -30.7) * mm, "end": v(21.34, -29.38) * mm});
            skLineSegment(sketch, "E15.51.18.0", {"start": v(25.4, -28.2) * mm, "end": v(24.3, -26.99) * mm});
            skPoint(sketch, "E15.1.19.0", {"position": v(28.77, -20.9) * mm});
            skPoint(sketch, "E15.2.19.0", {"position": v(30.82, -22.4) * mm});
            skArc(sketch, "E15.3.19.0", {"start": v(25.92, -24.34) * mm, "mid": v(27.64, -22.38) * mm, "end": v(29.2, -20.3) * mm});
            skPoint(sketch, "E15.7.19.0", {"position": v(28.31, -25.5) * mm});
            skPoint(sketch, "E15.8.19.0", {"position": v(26.43, -23.8) * mm});
            skPoint(sketch, "E15.9.19.0", {"position": v(31.15, -26.1) * mm});
            skArc(sketch, "E15.10.19.0", {"start": v(30.9, -22.52) * mm, "mid": v(31.47, -23.56) * mm, "end": v(31.9, -24.66) * mm});
            skArc(sketch, "E15.14.19.0", {"start": v(28.45, -25.55) * mm, "mid": v(29.59, -25.88) * mm, "end": v(30.75, -26.08) * mm});
            skPoint(sketch, "E15.15.19.0", {"position": v(32.01, -25.04) * mm});
            skArc(sketch, "E15.18.19.0", {"start": v(26.99, -24.3) * mm, "mid": v(26.44, -24.1) * mm, "end": v(25.92, -24.34) * mm});
            skArc(sketch, "E15.22.19.0", {"start": v(30.9, -22.52) * mm, "mid": v(30.82, -22.4) * mm, "end": v(30.7, -22.3) * mm});
            skArc(sketch, "E15.26.19.0", {"start": v(30.75, -26.08) * mm, "mid": v(31.1, -26.03) * mm, "end": v(31.4, -25.83) * mm});
            skLineSegment(sketch, "E15.30.19.0", {"start": v(31.8, -25.34) * mm, "end": v(31.6, -25.6) * mm});
            skArc(sketch, "E15.33.19.0", {"start": v(28.2, -25.4) * mm, "mid": v(28.32, -25.48) * mm, "end": v(28.45, -25.55) * mm});
            skArc(sketch, "E15.37.19.0", {"start": v(31.8, -25.34) * mm, "mid": v(31.93, -25.01) * mm, "end": v(31.9, -24.66) * mm});
            skLineSegment(sketch, "E15.41.19.0", {"start": v(31.4, -25.83) * mm, "end": v(31.6, -25.6) * mm});
            skArc(sketch, "E15.44.19.0", {"start": v(29.2, -20.3) * mm, "mid": v(29.08, -20.86) * mm, "end": v(29.38, -21.34) * mm});
            skLineSegment(sketch, "E15.48.19.0", {"start": v(28.2, -25.4) * mm, "end": v(26.99, -24.3) * mm});
            skLineSegment(sketch, "E15.51.19.0", {"start": v(30.7, -22.3) * mm, "end": v(29.38, -21.34) * mm});
            skPoint(sketch, "E15.1.20.0", {"position": v(32.49, -14.46) * mm});
            skPoint(sketch, "E15.2.20.0", {"position": v(34.8, -15.5) * mm});
            skArc(sketch, "E15.3.20.0", {"start": v(30.42, -18.42) * mm, "mid": v(31.68, -16.14) * mm, "end": v(32.78, -13.78) * mm});
            skPoint(sketch, "E15.7.20.0", {"position": v(33, -19.05) * mm});
            skPoint(sketch, "E15.8.20.0", {"position": v(30.8, -17.78) * mm});
            skPoint(sketch, "E15.9.20.0", {"position": v(35.9, -19.06) * mm});
            skArc(sketch, "E15.10.20.0", {"start": v(34.91, -15.6) * mm, "mid": v(35.68, -16.5) * mm, "end": v(36.33, -17.49) * mm});
            skArc(sketch, "E15.14.20.0", {"start": v(33.14, -19.07) * mm, "mid": v(34.32, -19.17) * mm, "end": v(35.5, -19.11) * mm});
            skPoint(sketch, "E15.15.20.0", {"position": v(36.52, -17.83) * mm});
            skArc(sketch, "E15.18.20.0", {"start": v(31.45, -18.16) * mm, "mid": v(30.88, -18.08) * mm, "end": v(30.42, -18.42) * mm});
            skArc(sketch, "E15.22.20.0", {"start": v(34.91, -15.6) * mm, "mid": v(34.8, -15.5) * mm, "end": v(34.67, -15.44) * mm});
            skArc(sketch, "E15.26.20.0", {"start": v(35.5, -19.11) * mm, "mid": v(35.84, -19) * mm, "end": v(36.08, -18.73) * mm});
            skLineSegment(sketch, "E15.30.20.0", {"start": v(36.36, -18.18) * mm, "end": v(36.24, -18.46) * mm});
            skArc(sketch, "E15.33.20.0", {"start": v(32.87, -18.98) * mm, "mid": v(33, -19.04) * mm, "end": v(33.14, -19.07) * mm});
            skArc(sketch, "E15.37.20.0", {"start": v(36.36, -18.18) * mm, "mid": v(36.43, -17.83) * mm, "end": v(36.33, -17.49) * mm});
            skLineSegment(sketch, "E15.41.20.0", {"start": v(36.08, -18.73) * mm, "end": v(36.24, -18.46) * mm});
            skArc(sketch, "E15.44.20.0", {"start": v(32.78, -13.78) * mm, "mid": v(32.78, -14.35) * mm, "end": v(33.17, -14.77) * mm});
            skLineSegment(sketch, "E15.48.20.0", {"start": v(32.87, -18.98) * mm, "end": v(31.45, -18.16) * mm});
            skLineSegment(sketch, "E15.51.20.0", {"start": v(34.67, -15.44) * mm, "end": v(33.17, -14.77) * mm});
            skPoint(sketch, "E15.1.21.0", {"position": v(34.78, -7.4) * mm});
            skPoint(sketch, "E15.2.21.0", {"position": v(37.27, -7.92) * mm});
            skArc(sketch, "E15.3.21.0", {"start": v(33.58, -11.7) * mm, "mid": v(34.35, -9.2) * mm, "end": v(34.93, -6.66) * mm});
            skPoint(sketch, "E15.7.21.0", {"position": v(36.24, -11.77) * mm});
            skPoint(sketch, "E15.8.21.0", {"position": v(33.82, -10.99) * mm});
            skPoint(sketch, "E15.9.21.0", {"position": v(39.07, -11.18) * mm});
            skArc(sketch, "E15.10.21.0", {"start": v(37.4, -8) * mm, "mid": v(38.33, -8.72) * mm, "end": v(39.17, -9.55) * mm});
            skArc(sketch, "E15.14.21.0", {"start": v(36.39, -11.76) * mm, "mid": v(37.56, -11.61) * mm, "end": v(38.7, -11.31) * mm});
            skPoint(sketch, "E15.15.21.0", {"position": v(39.43, -9.85) * mm});
            skArc(sketch, "E15.18.21.0", {"start": v(34.54, -11.22) * mm, "mid": v(33.96, -11.26) * mm, "end": v(33.58, -11.7) * mm});
            skArc(sketch, "E15.22.21.0", {"start": v(37.4, -8) * mm, "mid": v(37.27, -7.94) * mm, "end": v(37.13, -7.9) * mm});
            skArc(sketch, "E15.26.21.0", {"start": v(38.7, -11.31) * mm, "mid": v(39, -11.13) * mm, "end": v(39.19, -10.82) * mm});
            skLineSegment(sketch, "E15.30.21.0", {"start": v(39.35, -10.22) * mm, "end": v(39.28, -10.53) * mm});
            skArc(sketch, "E15.33.21.0", {"start": v(36.1, -11.73) * mm, "mid": v(36.24, -11.76) * mm, "end": v(36.39, -11.76) * mm});
            skArc(sketch, "E15.37.21.0", {"start": v(39.35, -10.22) * mm, "mid": v(39.34, -9.87) * mm, "end": v(39.17, -9.55) * mm});
            skLineSegment(sketch, "E15.41.21.0", {"start": v(39.19, -10.82) * mm, "end": v(39.28, -10.53) * mm});
            skArc(sketch, "E15.44.21.0", {"start": v(34.93, -6.66) * mm, "mid": v(35.04, -7.23) * mm, "end": v(35.52, -7.55) * mm});
            skLineSegment(sketch, "E15.48.21.0", {"start": v(36.1, -11.73) * mm, "end": v(34.54, -11.22) * mm});
            skLineSegment(sketch, "E15.51.21.0", {"start": v(37.13, -7.9) * mm, "end": v(35.52, -7.55) * mm});
            skPoint(sketch, "E15.1.22.0", {"position": v(35.56, 0) * mm});
            skPoint(sketch, "E15.2.22.0", {"position": v(38.1, 0) * mm});
            skArc(sketch, "E15.3.22.0", {"start": v(35.28, -4.46) * mm, "mid": v(35.51, -1.86) * mm, "end": v(35.55, 0.75) * mm});
            skPoint(sketch, "E15.7.22.0", {"position": v(37.9, -3.98) * mm});
            skPoint(sketch, "E15.8.22.0", {"position": v(35.37, -3.72) * mm});
            skPoint(sketch, "E15.9.22.0", {"position": v(40.54, -2.81) * mm});
            skArc(sketch, "E15.10.22.0", {"start": v(38.24, -0.06) * mm, "mid": v(39.3, -0.56) * mm, "end": v(40.3, -1.2) * mm});
            skArc(sketch, "E15.14.22.0", {"start": v(38.04, -3.94) * mm, "mid": v(39.15, -3.55) * mm, "end": v(40.2, -3.02) * mm});
            skPoint(sketch, "E15.15.22.0", {"position": v(40.61, -1.44) * mm});
            skArc(sketch, "E15.18.22.0", {"start": v(36.12, -3.8) * mm, "mid": v(35.56, -3.96) * mm, "end": v(35.28, -4.46) * mm});
            skArc(sketch, "E15.22.22.0", {"start": v(38.24, -0.06) * mm, "mid": v(38.1, -0.01) * mm, "end": v(37.96, 0) * mm});
            skArc(sketch, "E15.26.22.0", {"start": v(40.2, -3.02) * mm, "mid": v(40.46, -2.77) * mm, "end": v(40.58, -2.44) * mm});
            skLineSegment(sketch, "E15.30.22.0", {"start": v(40.61, -1.82) * mm, "end": v(40.61, -2.13) * mm});
            skArc(sketch, "E15.33.22.0", {"start": v(37.75, -3.97) * mm, "mid": v(37.9, -3.97) * mm, "end": v(38.04, -3.94) * mm});
            skArc(sketch, "E15.37.22.0", {"start": v(40.61, -1.82) * mm, "mid": v(40.53, -1.47) * mm, "end": v(40.3, -1.2) * mm});
            skLineSegment(sketch, "E15.41.22.0", {"start": v(40.58, -2.44) * mm, "end": v(40.61, -2.13) * mm});
            skArc(sketch, "E15.44.22.0", {"start": v(35.55, 0.75) * mm, "mid": v(35.78, 0.22) * mm, "end": v(36.31, 0) * mm});
            skLineSegment(sketch, "E15.48.22.0", {"start": v(37.75, -3.97) * mm, "end": v(36.12, -3.8) * mm});
            skLineSegment(sketch, "E15.51.22.0", {"start": v(37.96, 0) * mm, "end": v(36.31, 0) * mm});
            skPoint(sketch, "E15.1.23.0", {"position": v(34.78, 7.4) * mm});
            skPoint(sketch, "E15.2.23.0", {"position": v(37.27, 7.92) * mm});
            skArc(sketch, "E15.3.23.0", {"start": v(35.44, 2.97) * mm, "mid": v(35.12, 5.56) * mm, "end": v(34.62, 8.12) * mm});
            skPoint(sketch, "E15.7.23.0", {"position": v(37.9, 3.98) * mm});
            skPoint(sketch, "E15.8.23.0", {"position": v(35.37, 3.72) * mm});
            skPoint(sketch, "E15.9.23.0", {"position": v(40.24, 5.68) * mm});
            skArc(sketch, "E15.10.23.0", {"start": v(37.42, 7.9) * mm, "mid": v(38.57, 7.62) * mm, "end": v(39.67, 7.2) * mm});
            skArc(sketch, "E15.14.23.0", {"start": v(38.02, 4.05) * mm, "mid": v(39.03, 4.67) * mm, "end": v(39.96, 5.4) * mm});
            skPoint(sketch, "E15.15.23.0", {"position": v(40.03, 7.04) * mm});
            skArc(sketch, "E15.18.23.0", {"start": v(36.12, 3.8) * mm, "mid": v(35.6, 3.52) * mm, "end": v(35.44, 2.97) * mm});
            skArc(sketch, "E15.22.23.0", {"start": v(37.42, 7.9) * mm, "mid": v(37.27, 7.9) * mm, "end": v(37.13, 7.9) * mm});
            skArc(sketch, "E15.26.23.0", {"start": v(39.96, 5.4) * mm, "mid": v(40.16, 5.7) * mm, "end": v(40.2, 6.05) * mm});
            skLineSegment(sketch, "E15.30.23.0", {"start": v(40.1, 6.67) * mm, "end": v(40.17, 6.36) * mm});
            skArc(sketch, "E15.33.23.0", {"start": v(37.75, 3.97) * mm, "mid": v(37.9, 4) * mm, "end": v(38.02, 4.05) * mm});
            skArc(sketch, "E15.37.23.0", {"start": v(40.1, 6.67) * mm, "mid": v(39.95, 6.99) * mm, "end": v(39.67, 7.2) * mm});
            skLineSegment(sketch, "E15.41.23.0", {"start": v(40.2, 6.05) * mm, "end": v(40.17, 6.36) * mm});
            skArc(sketch, "E15.44.23.0", {"start": v(34.62, 8.12) * mm, "mid": v(34.95, 7.65) * mm, "end": v(35.52, 7.55) * mm});
            skLineSegment(sketch, "E15.48.23.0", {"start": v(37.75, 3.97) * mm, "end": v(36.12, 3.8) * mm});
            skLineSegment(sketch, "E15.51.23.0", {"start": v(37.13, 7.9) * mm, "end": v(35.52, 7.55) * mm});
            skPoint(sketch, "E15.1.24.0", {"position": v(32.49, 14.46) * mm});
            skPoint(sketch, "E15.2.24.0", {"position": v(34.8, 15.5) * mm});
            skArc(sketch, "E15.3.24.0", {"start": v(34.04, 10.28) * mm, "mid": v(33.2, 12.74) * mm, "end": v(32.18, 15.14) * mm});
            skPoint(sketch, "E15.7.24.0", {"position": v(36.24, 11.77) * mm});
            skPoint(sketch, "E15.8.24.0", {"position": v(33.82, 10.99) * mm});
            skPoint(sketch, "E15.9.24.0", {"position": v(38.18, 13.92) * mm});
            skArc(sketch, "E15.10.24.0", {"start": v(34.96, 15.5) * mm, "mid": v(36.14, 15.47) * mm, "end": v(37.3, 15.3) * mm});
            skArc(sketch, "E15.14.24.0", {"start": v(36.35, 11.87) * mm, "mid": v(37.2, 12.68) * mm, "end": v(37.96, 13.6) * mm});
            skPoint(sketch, "E15.15.24.0", {"position": v(37.69, 15.2) * mm});
            skArc(sketch, "E15.18.24.0", {"start": v(34.54, 11.22) * mm, "mid": v(34.1, 10.85) * mm, "end": v(34.04, 10.28) * mm});
            skArc(sketch, "E15.22.24.0", {"start": v(34.96, 15.5) * mm, "mid": v(34.81, 15.48) * mm, "end": v(34.67, 15.44) * mm});
            skArc(sketch, "E15.26.24.0", {"start": v(37.96, 13.6) * mm, "mid": v(38.1, 13.92) * mm, "end": v(38.07, 14.28) * mm});
            skLineSegment(sketch, "E15.30.24.0", {"start": v(37.84, 14.86) * mm, "end": v(37.97, 14.57) * mm});
            skArc(sketch, "E15.33.24.0", {"start": v(36.1, 11.73) * mm, "mid": v(36.23, 11.79) * mm, "end": v(36.35, 11.87) * mm});
            skArc(sketch, "E15.37.24.0", {"start": v(37.84, 14.86) * mm, "mid": v(37.63, 15.14) * mm, "end": v(37.3, 15.3) * mm});
            skLineSegment(sketch, "E15.41.24.0", {"start": v(38.07, 14.28) * mm, "end": v(37.97, 14.57) * mm});
            skArc(sketch, "E15.44.24.0", {"start": v(32.18, 15.14) * mm, "mid": v(32.6, 14.75) * mm, "end": v(33.17, 14.77) * mm});
            skLineSegment(sketch, "E15.48.24.0", {"start": v(36.1, 11.73) * mm, "end": v(34.54, 11.22) * mm});
            skLineSegment(sketch, "E15.51.24.0", {"start": v(34.67, 15.44) * mm, "end": v(33.17, 14.77) * mm});
            skPoint(sketch, "E15.1.25.0", {"position": v(28.77, 20.9) * mm});
            skPoint(sketch, "E15.2.25.0", {"position": v(30.82, 22.4) * mm});
            skArc(sketch, "E15.3.25.0", {"start": v(31.16, 17.13) * mm, "mid": v(29.82, 19.37) * mm, "end": v(28.32, 21.5) * mm});
            skPoint(sketch, "E15.7.25.0", {"position": v(33, 19.05) * mm});
            skPoint(sketch, "E15.8.25.0", {"position": v(30.8, 17.78) * mm});
            skPoint(sketch, "E15.9.25.0", {"position": v(34.45, 21.55) * mm});
            skArc(sketch, "E15.10.25.0", {"start": v(30.97, 22.43) * mm, "mid": v(32.13, 22.65) * mm, "end": v(33.31, 22.72) * mm});
            skArc(sketch, "E15.14.25.0", {"start": v(33.09, 19.17) * mm, "mid": v(33.76, 20.14) * mm, "end": v(34.3, 21.2) * mm});
            skPoint(sketch, "E15.15.25.0", {"position": v(33.7, 22.7) * mm});
            skArc(sketch, "E15.18.25.0", {"start": v(31.45, 18.16) * mm, "mid": v(31.1, 17.7) * mm, "end": v(31.16, 17.13) * mm});
            skArc(sketch, "E15.22.25.0", {"start": v(30.97, 22.43) * mm, "mid": v(30.83, 22.38) * mm, "end": v(30.7, 22.3) * mm});
            skArc(sketch, "E15.26.25.0", {"start": v(34.3, 21.2) * mm, "mid": v(34.37, 21.54) * mm, "end": v(34.27, 21.88) * mm});
            skLineSegment(sketch, "E15.30.25.0", {"start": v(33.93, 22.4) * mm, "end": v(34.1, 22.15) * mm});
            skArc(sketch, "E15.33.25.0", {"start": v(32.87, 18.98) * mm, "mid": v(32.99, 19.06) * mm, "end": v(33.09, 19.17) * mm});
            skArc(sketch, "E15.37.25.0", {"start": v(33.93, 22.4) * mm, "mid": v(33.66, 22.63) * mm, "end": v(33.31, 22.72) * mm});
            skLineSegment(sketch, "E15.41.25.0", {"start": v(34.27, 21.88) * mm, "end": v(34.1, 22.15) * mm});
            skArc(sketch, "E15.44.25.0", {"start": v(28.32, 21.5) * mm, "mid": v(28.82, 21.2) * mm, "end": v(29.38, 21.34) * mm});
            skLineSegment(sketch, "E15.48.25.0", {"start": v(32.87, 18.98) * mm, "end": v(31.45, 18.16) * mm});
            skLineSegment(sketch, "E15.51.25.0", {"start": v(30.7, 22.3) * mm, "end": v(29.38, 21.34) * mm});
            skPoint(sketch, "E15.1.26.0", {"position": v(23.8, 26.43) * mm});
            skPoint(sketch, "E15.2.26.0", {"position": v(25.5, 28.31) * mm});
            skArc(sketch, "E15.3.26.0", {"start": v(26.92, 23.23) * mm, "mid": v(25.14, 25.14) * mm, "end": v(23.23, 26.92) * mm});
            skPoint(sketch, "E15.7.26.0", {"position": v(28.31, 25.5) * mm});
            skPoint(sketch, "E15.8.26.0", {"position": v(26.43, 23.8) * mm});
            skPoint(sketch, "E15.9.26.0", {"position": v(29.22, 28.25) * mm});
            skArc(sketch, "E15.10.26.0", {"start": v(25.63, 28.38) * mm, "mid": v(26.72, 28.83) * mm, "end": v(27.86, 29.15) * mm});
            skArc(sketch, "E15.14.26.0", {"start": v(28.38, 25.63) * mm, "mid": v(28.83, 26.72) * mm, "end": v(29.15, 27.86) * mm});
            skPoint(sketch, "E15.15.26.0", {"position": v(28.25, 29.22) * mm});
            skArc(sketch, "E15.18.26.0", {"start": v(26.99, 24.3) * mm, "mid": v(26.74, 23.78) * mm, "end": v(26.92, 23.23) * mm});
            skArc(sketch, "E15.22.26.0", {"start": v(25.63, 28.38) * mm, "mid": v(25.5, 28.3) * mm, "end": v(25.4, 28.2) * mm});
            skArc(sketch, "E15.26.26.0", {"start": v(29.15, 27.86) * mm, "mid": v(29.14, 28.21) * mm, "end": v(28.97, 28.53) * mm});
            skLineSegment(sketch, "E15.30.26.0", {"start": v(28.53, 28.97) * mm, "end": v(28.76, 28.76) * mm});
            skArc(sketch, "E15.33.26.0", {"start": v(28.2, 25.4) * mm, "mid": v(28.3, 25.5) * mm, "end": v(28.38, 25.63) * mm});
            skArc(sketch, "E15.37.26.0", {"start": v(28.53, 28.97) * mm, "mid": v(28.21, 29.14) * mm, "end": v(27.86, 29.15) * mm});
            skLineSegment(sketch, "E15.41.26.0", {"start": v(28.97, 28.53) * mm, "end": v(28.76, 28.76) * mm});
            skArc(sketch, "E15.44.26.0", {"start": v(23.23, 26.92) * mm, "mid": v(23.78, 26.74) * mm, "end": v(24.3, 26.99) * mm});
            skLineSegment(sketch, "E15.48.26.0", {"start": v(28.2, 25.4) * mm, "end": v(26.99, 24.3) * mm});
            skLineSegment(sketch, "E15.51.26.0", {"start": v(25.4, 28.2) * mm, "end": v(24.3, 26.99) * mm});
            skPoint(sketch, "E15.1.27.0", {"position": v(17.78, 30.8) * mm});
            skPoint(sketch, "E15.2.27.0", {"position": v(19.05, 33) * mm});
            skArc(sketch, "E15.3.27.0", {"start": v(21.5, 28.32) * mm, "mid": v(19.37, 29.82) * mm, "end": v(17.13, 31.16) * mm});
            skPoint(sketch, "E15.7.27.0", {"position": v(22.4, 30.82) * mm});
            skPoint(sketch, "E15.8.27.0", {"position": v(20.9, 28.77) * mm});
            skPoint(sketch, "E15.9.27.0", {"position": v(22.7, 33.7) * mm});
            skArc(sketch, "E15.10.27.0", {"start": v(19.17, 33.09) * mm, "mid": v(20.14, 33.76) * mm, "end": v(21.2, 34.3) * mm});
            skArc(sketch, "E15.14.27.0", {"start": v(22.43, 30.97) * mm, "mid": v(22.65, 32.13) * mm, "end": v(22.72, 33.31) * mm});
            skPoint(sketch, "E15.15.27.0", {"position": v(21.55, 34.45) * mm});
            skArc(sketch, "E15.18.27.0", {"start": v(21.34, 29.38) * mm, "mid": v(21.2, 28.82) * mm, "end": v(21.5, 28.32) * mm});
            skArc(sketch, "E15.22.27.0", {"start": v(19.17, 33.09) * mm, "mid": v(19.06, 32.99) * mm, "end": v(18.98, 32.87) * mm});
            skArc(sketch, "E15.26.27.0", {"start": v(22.72, 33.31) * mm, "mid": v(22.63, 33.66) * mm, "end": v(22.4, 33.93) * mm});
            skLineSegment(sketch, "E15.30.27.0", {"start": v(21.88, 34.27) * mm, "end": v(22.15, 34.1) * mm});
            skArc(sketch, "E15.33.27.0", {"start": v(22.3, 30.7) * mm, "mid": v(22.38, 30.83) * mm, "end": v(22.43, 30.97) * mm});
            skArc(sketch, "E15.37.27.0", {"start": v(21.88, 34.27) * mm, "mid": v(21.54, 34.37) * mm, "end": v(21.2, 34.3) * mm});
            skLineSegment(sketch, "E15.41.27.0", {"start": v(22.4, 33.93) * mm, "end": v(22.15, 34.1) * mm});
            skArc(sketch, "E15.44.27.0", {"start": v(17.13, 31.16) * mm, "mid": v(17.7, 31.1) * mm, "end": v(18.16, 31.45) * mm});
            skLineSegment(sketch, "E15.48.27.0", {"start": v(22.3, 30.7) * mm, "end": v(21.34, 29.38) * mm});
            skLineSegment(sketch, "E15.51.27.0", {"start": v(18.98, 32.87) * mm, "end": v(18.16, 31.45) * mm});
            skPoint(sketch, "E15.1.28.0", {"position": v(10.99, 33.82) * mm});
            skPoint(sketch, "E15.2.28.0", {"position": v(11.77, 36.24) * mm});
            skArc(sketch, "E15.3.28.0", {"start": v(15.14, 32.18) * mm, "mid": v(12.74, 33.2) * mm, "end": v(10.28, 34.04) * mm});
            skPoint(sketch, "E15.7.28.0", {"position": v(15.5, 34.8) * mm});
            skPoint(sketch, "E15.8.28.0", {"position": v(14.46, 32.49) * mm});
            skPoint(sketch, "E15.9.28.0", {"position": v(15.2, 37.69) * mm});
            skArc(sketch, "E15.10.28.0", {"start": v(11.87, 36.35) * mm, "mid": v(12.68, 37.2) * mm, "end": v(13.6, 37.96) * mm});
            skArc(sketch, "E15.14.28.0", {"start": v(15.5, 34.96) * mm, "mid": v(15.47, 36.14) * mm, "end": v(15.3, 37.3) * mm});
            skPoint(sketch, "E15.15.28.0", {"position": v(13.92, 38.18) * mm});
            skArc(sketch, "E15.18.28.0", {"start": v(14.77, 33.17) * mm, "mid": v(14.75, 32.6) * mm, "end": v(15.14, 32.18) * mm});
            skArc(sketch, "E15.22.28.0", {"start": v(11.87, 36.35) * mm, "mid": v(11.79, 36.23) * mm, "end": v(11.73, 36.1) * mm});
            skArc(sketch, "E15.26.28.0", {"start": v(15.3, 37.3) * mm, "mid": v(15.14, 37.63) * mm, "end": v(14.86, 37.84) * mm});
            skLineSegment(sketch, "E15.30.28.0", {"start": v(14.28, 38.07) * mm, "end": v(14.57, 37.97) * mm});
            skArc(sketch, "E15.33.28.0", {"start": v(15.44, 34.67) * mm, "mid": v(15.48, 34.81) * mm, "end": v(15.5, 34.96) * mm});
            skArc(sketch, "E15.37.28.0", {"start": v(14.28, 38.07) * mm, "mid": v(13.92, 38.1) * mm, "end": v(13.6, 37.96) * mm});
            skLineSegment(sketch, "E15.41.28.0", {"start": v(14.86, 37.84) * mm, "end": v(14.57, 37.97) * mm});
            skArc(sketch, "E15.44.28.0", {"start": v(10.28, 34.04) * mm, "mid": v(10.85, 34.1) * mm, "end": v(11.22, 34.54) * mm});
            skLineSegment(sketch, "E15.48.28.0", {"start": v(15.44, 34.67) * mm, "end": v(14.77, 33.17) * mm});
            skLineSegment(sketch, "E15.51.28.0", {"start": v(11.73, 36.1) * mm, "end": v(11.22, 34.54) * mm});
            skPoint(sketch, "E15.1.29.0", {"position": v(3.72, 35.37) * mm});
            skPoint(sketch, "E15.2.29.0", {"position": v(3.98, 37.9) * mm});
            skArc(sketch, "E15.3.29.0", {"start": v(8.12, 34.62) * mm, "mid": v(5.56, 35.12) * mm, "end": v(2.97, 35.44) * mm});
            skPoint(sketch, "E15.7.29.0", {"position": v(7.92, 37.27) * mm});
            skPoint(sketch, "E15.8.29.0", {"position": v(7.4, 34.78) * mm});
            skPoint(sketch, "E15.9.29.0", {"position": v(7.04, 40.03) * mm});
            skArc(sketch, "E15.10.29.0", {"start": v(4.05, 38.02) * mm, "mid": v(4.67, 39.03) * mm, "end": v(5.4, 39.96) * mm});
            skArc(sketch, "E15.14.29.0", {"start": v(7.9, 37.42) * mm, "mid": v(7.62, 38.57) * mm, "end": v(7.2, 39.67) * mm});
            skPoint(sketch, "E15.15.29.0", {"position": v(5.68, 40.24) * mm});
            skArc(sketch, "E15.18.29.0", {"start": v(7.55, 35.52) * mm, "mid": v(7.65, 34.95) * mm, "end": v(8.12, 34.62) * mm});
            skArc(sketch, "E15.22.29.0", {"start": v(4.05, 38.02) * mm, "mid": v(4, 37.9) * mm, "end": v(3.97, 37.75) * mm});
            skArc(sketch, "E15.26.29.0", {"start": v(7.2, 39.67) * mm, "mid": v(6.99, 39.95) * mm, "end": v(6.67, 40.1) * mm});
            skLineSegment(sketch, "E15.30.29.0", {"start": v(6.05, 40.2) * mm, "end": v(6.36, 40.17) * mm});
            skArc(sketch, "E15.33.29.0", {"start": v(7.9, 37.13) * mm, "mid": v(7.9, 37.27) * mm, "end": v(7.9, 37.42) * mm});
            skArc(sketch, "E15.37.29.0", {"start": v(6.05, 40.2) * mm, "mid": v(5.7, 40.16) * mm, "end": v(5.4, 39.96) * mm});
            skLineSegment(sketch, "E15.41.29.0", {"start": v(6.67, 40.1) * mm, "end": v(6.36, 40.17) * mm});
            skArc(sketch, "E15.44.29.0", {"start": v(2.97, 35.44) * mm, "mid": v(3.52, 35.6) * mm, "end": v(3.8, 36.12) * mm});
            skLineSegment(sketch, "E15.48.29.0", {"start": v(7.9, 37.13) * mm, "end": v(7.55, 35.52) * mm});
            skLineSegment(sketch, "E15.51.29.0", {"start": v(3.97, 37.75) * mm, "end": v(3.8, 36.12) * mm});
            skSolve(sketch);
        }
        {
            var Q0;
            Q0 = qSketchRegion(id + "F2", true);
            extrude(context, id + "F3", {"entities" : qUnion([Q0]), "operationType" : NewBodyOperationType.ADD, "oppositeDirection" : true, "depth" : 114.3 * mm});
        }
        {
            var Q0;
            Q0=makeQuery(id+"F3.boolean.opBoolean","MERGE",FACE,{"derivedFrom":[makeQuery(id+"F1.opExtrude","CAP_FACE",FACE,{"disambiguationData":[OSD([sQuery(id+"F0.wireOp",EDGE,"E0")])],"isStart":false}),makeQuery(id+"F3.opExtrude","CAP_FACE",FACE,{"disambiguationData":[OSD([sQuery(id+"F2.wireOp",EDGE,"E1.trimOffspring"),sQuery(id+"F2.wireOp",EDGE,"E2"),sQuery(id+"F2.wireOp",EDGE,"E3"),sQuery(id+"F2.wireOp",EDGE,"E4.MirrorCS"),sQuery(id+"F2.wireOp",EDGE,"E5.MirrorCS"),sQuery(id+"F2.wireOp",EDGE,"E6.MirrorCS"),sQuery(id+"F2.wireOp",EDGE,"E7.filletArc"),sQuery(id+"F2.wireOp",EDGE,"E8.filletArc"),sQuery(id+"F2.wireOp",EDGE,"E9.filletArc"),sQuery(id+"F2.wireOp",EDGE,"E10.filletArc"),sQuery(id+"F2.wireOp",EDGE,"E11.filletArc"),sQuery(id+"F2.wireOp",EDGE,"E12.filletArc"),sQuery(id+"F2.wireOp",EDGE,"E13")])],"isStart":true}),makeQuery(id+"F3.opExtrude","CAP_FACE",FACE,{"disambiguationData":[OSD([sQuery(id+"F2.wireOp",EDGE,"E14.1.3"),sQuery(id+"F2.wireOp",EDGE,"E14.1.7"),sQuery(id+"F2.wireOp",EDGE,"E14.1.8"),sQuery(id+"F2.wireOp",EDGE,"E14.1.9"),sQuery(id+"F2.wireOp",EDGE,"E14.1.10"),sQuery(id+"F2.wireOp",EDGE,"E14.1.11"),sQuery(id+"F2.wireOp",EDGE,"E14.1.12"),sQuery(id+"F2.wireOp",EDGE,"E14.1.13"),sQuery(id+"F2.wireOp",EDGE,"E14.1.14"),sQuery(id+"F2.wireOp",EDGE,"E14.1.15"),sQuery(id+"F2.wireOp",EDGE,"E14.1.16"),sQuery(id+"F2.wireOp",EDGE,"E14.1.17"),sQuery(id+"F2.wireOp",EDGE,"E14.1.18")])],"isStart":true}),makeQuery(id+"F3.opExtrude","CAP_FACE",FACE,{"disambiguationData":[OSD([sQuery(id+"F2.wireOp",EDGE,"E14.2.3"),sQuery(id+"F2.wireOp",EDGE,"E14.2.7"),sQuery(id+"F2.wireOp",EDGE,"E14.2.8"),sQuery(id+"F2.wireOp",EDGE,"E14.2.9"),sQuery(id+"F2.wireOp",EDGE,"E14.2.10"),sQuery(id+"F2.wireOp",EDGE,"E14.2.11"),sQuery(id+"F2.wireOp",EDGE,"E14.2.12"),sQuery(id+"F2.wireOp",EDGE,"E14.2.13"),sQuery(id+"F2.wireOp",EDGE,"E14.2.14"),sQuery(id+"F2.wireOp",EDGE,"E14.2.15"),sQuery(id+"F2.wireOp",EDGE,"E14.2.16"),sQuery(id+"F2.wireOp",EDGE,"E14.2.17"),sQuery(id+"F2.wireOp",EDGE,"E14.2.18")])],"isStart":true}),makeQuery(id+"F3.opExtrude","CAP_FACE",FACE,{"disambiguationData":[OSD([sQuery(id+"F2.wireOp",EDGE,"E15.3.3.0"),sQuery(id+"F2.wireOp",EDGE,"E15.10.3.0"),sQuery(id+"F2.wireOp",EDGE,"E15.14.3.0"),sQuery(id+"F2.wireOp",EDGE,"E15.18.3.0"),sQuery(id+"F2.wireOp",EDGE,"E15.22.3.0"),sQuery(id+"F2.wireOp",EDGE,"E15.26.3.0"),sQuery(id+"F2.wireOp",EDGE,"E15.30.3.0"),sQuery(id+"F2.wireOp",EDGE,"E15.33.3.0"),sQuery(id+"F2.wireOp",EDGE,"E15.37.3.0"),sQuery(id+"F2.wireOp",EDGE,"E15.41.3.0"),sQuery(id+"F2.wireOp",EDGE,"E15.44.3.0"),sQuery(id+"F2.wireOp",EDGE,"E15.48.3.0"),sQuery(id+"F2.wireOp",EDGE,"E15.51.3.0")])],"isStart":true}),makeQuery(id+"F3.opExtrude","CAP_FACE",FACE,{"disambiguationData":[OSD([sQuery(id+"F2.wireOp",EDGE,"E15.3.4.0"),sQuery(id+"F2.wireOp",EDGE,"E15.10.4.0"),sQuery(id+"F2.wireOp",EDGE,"E15.14.4.0"),sQuery(id+"F2.wireOp",EDGE,"E15.18.4.0"),sQuery(id+"F2.wireOp",EDGE,"E15.22.4.0"),sQuery(id+"F2.wireOp",EDGE,"E15.26.4.0"),sQuery(id+"F2.wireOp",EDGE,"E15.30.4.0"),sQuery(id+"F2.wireOp",EDGE,"E15.33.4.0"),sQuery(id+"F2.wireOp",EDGE,"E15.37.4.0"),sQuery(id+"F2.wireOp",EDGE,"E15.41.4.0"),sQuery(id+"F2.wireOp",EDGE,"E15.44.4.0"),sQuery(id+"F2.wireOp",EDGE,"E15.48.4.0"),sQuery(id+"F2.wireOp",EDGE,"E15.51.4.0")])],"isStart":true}),makeQuery(id+"F3.opExtrude","CAP_FACE",FACE,{"disambiguationData":[OSD([sQuery(id+"F2.wireOp",EDGE,"E15.3.5.0"),sQuery(id+"F2.wireOp",EDGE,"E15.10.5.0"),sQuery(id+"F2.wireOp",EDGE,"E15.14.5.0"),sQuery(id+"F2.wireOp",EDGE,"E15.18.5.0"),sQuery(id+"F2.wireOp",EDGE,"E15.22.5.0"),sQuery(id+"F2.wireOp",EDGE,"E15.26.5.0"),sQuery(id+"F2.wireOp",EDGE,"E15.30.5.0"),sQuery(id+"F2.wireOp",EDGE,"E15.33.5.0"),sQuery(id+"F2.wireOp",EDGE,"E15.37.5.0"),sQuery(id+"F2.wireOp",EDGE,"E15.41.5.0"),sQuery(id+"F2.wireOp",EDGE,"E15.44.5.0"),sQuery(id+"F2.wireOp",EDGE,"E15.48.5.0"),sQuery(id+"F2.wireOp",EDGE,"E15.51.5.0")])],"isStart":true}),makeQuery(id+"F3.opExtrude","CAP_FACE",FACE,{"disambiguationData":[OSD([sQuery(id+"F2.wireOp",EDGE,"E15.3.6.0"),sQuery(id+"F2.wireOp",EDGE,"E15.10.6.0"),sQuery(id+"F2.wireOp",EDGE,"E15.14.6.0"),sQuery(id+"F2.wireOp",EDGE,"E15.18.6.0"),sQuery(id+"F2.wireOp",EDGE,"E15.22.6.0"),sQuery(id+"F2.wireOp",EDGE,"E15.26.6.0"),sQuery(id+"F2.wireOp",EDGE,"E15.30.6.0"),sQuery(id+"F2.wireOp",EDGE,"E15.33.6.0"),sQuery(id+"F2.wireOp",EDGE,"E15.37.6.0"),sQuery(id+"F2.wireOp",EDGE,"E15.41.6.0"),sQuery(id+"F2.wireOp",EDGE,"E15.44.6.0"),sQuery(id+"F2.wireOp",EDGE,"E15.48.6.0"),sQuery(id+"F2.wireOp",EDGE,"E15.51.6.0")])],"isStart":true}),makeQuery(id+"F3.opExtrude","CAP_FACE",FACE,{"disambiguationData":[OSD([sQuery(id+"F2.wireOp",EDGE,"E15.3.7.0"),sQuery(id+"F2.wireOp",EDGE,"E15.10.7.0"),sQuery(id+"F2.wireOp",EDGE,"E15.14.7.0"),sQuery(id+"F2.wireOp",EDGE,"E15.18.7.0"),sQuery(id+"F2.wireOp",EDGE,"E15.22.7.0"),sQuery(id+"F2.wireOp",EDGE,"E15.26.7.0"),sQuery(id+"F2.wireOp",EDGE,"E15.30.7.0"),sQuery(id+"F2.wireOp",EDGE,"E15.33.7.0"),sQuery(id+"F2.wireOp",EDGE,"E15.37.7.0"),sQuery(id+"F2.wireOp",EDGE,"E15.41.7.0"),sQuery(id+"F2.wireOp",EDGE,"E15.44.7.0"),sQuery(id+"F2.wireOp",EDGE,"E15.48.7.0"),sQuery(id+"F2.wireOp",EDGE,"E15.51.7.0")])],"isStart":true}),makeQuery(id+"F3.opExtrude","CAP_FACE",FACE,{"disambiguationData":[OSD([sQuery(id+"F2.wireOp",EDGE,"E15.3.8.0"),sQuery(id+"F2.wireOp",EDGE,"E15.10.8.0"),sQuery(id+"F2.wireOp",EDGE,"E15.14.8.0"),sQuery(id+"F2.wireOp",EDGE,"E15.18.8.0"),sQuery(id+"F2.wireOp",EDGE,"E15.22.8.0"),sQuery(id+"F2.wireOp",EDGE,"E15.26.8.0"),sQuery(id+"F2.wireOp",EDGE,"E15.30.8.0"),sQuery(id+"F2.wireOp",EDGE,"E15.33.8.0"),sQuery(id+"F2.wireOp",EDGE,"E15.37.8.0"),sQuery(id+"F2.wireOp",EDGE,"E15.41.8.0"),sQuery(id+"F2.wireOp",EDGE,"E15.44.8.0"),sQuery(id+"F2.wireOp",EDGE,"E15.48.8.0"),sQuery(id+"F2.wireOp",EDGE,"E15.51.8.0")])],"isStart":true}),makeQuery(id+"F3.opExtrude","CAP_FACE",FACE,{"disambiguationData":[OSD([sQuery(id+"F2.wireOp",EDGE,"E15.3.9.0"),sQuery(id+"F2.wireOp",EDGE,"E15.10.9.0"),sQuery(id+"F2.wireOp",EDGE,"E15.14.9.0"),sQuery(id+"F2.wireOp",EDGE,"E15.18.9.0"),sQuery(id+"F2.wireOp",EDGE,"E15.22.9.0"),sQuery(id+"F2.wireOp",EDGE,"E15.26.9.0"),sQuery(id+"F2.wireOp",EDGE,"E15.30.9.0"),sQuery(id+"F2.wireOp",EDGE,"E15.33.9.0"),sQuery(id+"F2.wireOp",EDGE,"E15.37.9.0"),sQuery(id+"F2.wireOp",EDGE,"E15.41.9.0"),sQuery(id+"F2.wireOp",EDGE,"E15.44.9.0"),sQuery(id+"F2.wireOp",EDGE,"E15.48.9.0"),sQuery(id+"F2.wireOp",EDGE,"E15.51.9.0")])],"isStart":true}),makeQuery(id+"F3.opExtrude","CAP_FACE",FACE,{"disambiguationData":[OSD([sQuery(id+"F2.wireOp",EDGE,"E15.3.10.0"),sQuery(id+"F2.wireOp",EDGE,"E15.10.10.0"),sQuery(id+"F2.wireOp",EDGE,"E15.14.10.0"),sQuery(id+"F2.wireOp",EDGE,"E15.18.10.0"),sQuery(id+"F2.wireOp",EDGE,"E15.22.10.0"),sQuery(id+"F2.wireOp",EDGE,"E15.26.10.0"),sQuery(id+"F2.wireOp",EDGE,"E15.30.10.0"),sQuery(id+"F2.wireOp",EDGE,"E15.33.10.0"),sQuery(id+"F2.wireOp",EDGE,"E15.37.10.0"),sQuery(id+"F2.wireOp",EDGE,"E15.41.10.0"),sQuery(id+"F2.wireOp",EDGE,"E15.44.10.0"),sQuery(id+"F2.wireOp",EDGE,"E15.48.10.0"),sQuery(id+"F2.wireOp",EDGE,"E15.51.10.0")])],"isStart":true}),makeQuery(id+"F3.opExtrude","CAP_FACE",FACE,{"disambiguationData":[OSD([sQuery(id+"F2.wireOp",EDGE,"E15.3.11.0"),sQuery(id+"F2.wireOp",EDGE,"E15.10.11.0"),sQuery(id+"F2.wireOp",EDGE,"E15.14.11.0"),sQuery(id+"F2.wireOp",EDGE,"E15.18.11.0"),sQuery(id+"F2.wireOp",EDGE,"E15.22.11.0"),sQuery(id+"F2.wireOp",EDGE,"E15.26.11.0"),sQuery(id+"F2.wireOp",EDGE,"E15.30.11.0"),sQuery(id+"F2.wireOp",EDGE,"E15.33.11.0"),sQuery(id+"F2.wireOp",EDGE,"E15.37.11.0"),sQuery(id+"F2.wireOp",EDGE,"E15.41.11.0"),sQuery(id+"F2.wireOp",EDGE,"E15.44.11.0"),sQuery(id+"F2.wireOp",EDGE,"E15.48.11.0"),sQuery(id+"F2.wireOp",EDGE,"E15.51.11.0")])],"isStart":true}),makeQuery(id+"F3.opExtrude","CAP_FACE",FACE,{"disambiguationData":[OSD([sQuery(id+"F2.wireOp",EDGE,"E15.3.12.0"),sQuery(id+"F2.wireOp",EDGE,"E15.10.12.0"),sQuery(id+"F2.wireOp",EDGE,"E15.14.12.0"),sQuery(id+"F2.wireOp",EDGE,"E15.18.12.0"),sQuery(id+"F2.wireOp",EDGE,"E15.22.12.0"),sQuery(id+"F2.wireOp",EDGE,"E15.26.12.0"),sQuery(id+"F2.wireOp",EDGE,"E15.30.12.0"),sQuery(id+"F2.wireOp",EDGE,"E15.33.12.0"),sQuery(id+"F2.wireOp",EDGE,"E15.37.12.0"),sQuery(id+"F2.wireOp",EDGE,"E15.41.12.0"),sQuery(id+"F2.wireOp",EDGE,"E15.44.12.0"),sQuery(id+"F2.wireOp",EDGE,"E15.48.12.0"),sQuery(id+"F2.wireOp",EDGE,"E15.51.12.0")])],"isStart":true}),makeQuery(id+"F3.opExtrude","CAP_FACE",FACE,{"disambiguationData":[OSD([sQuery(id+"F2.wireOp",EDGE,"E15.3.13.0"),sQuery(id+"F2.wireOp",EDGE,"E15.10.13.0"),sQuery(id+"F2.wireOp",EDGE,"E15.14.13.0"),sQuery(id+"F2.wireOp",EDGE,"E15.18.13.0"),sQuery(id+"F2.wireOp",EDGE,"E15.22.13.0"),sQuery(id+"F2.wireOp",EDGE,"E15.26.13.0"),sQuery(id+"F2.wireOp",EDGE,"E15.30.13.0"),sQuery(id+"F2.wireOp",EDGE,"E15.33.13.0"),sQuery(id+"F2.wireOp",EDGE,"E15.37.13.0"),sQuery(id+"F2.wireOp",EDGE,"E15.41.13.0"),sQuery(id+"F2.wireOp",EDGE,"E15.44.13.0"),sQuery(id+"F2.wireOp",EDGE,"E15.48.13.0"),sQuery(id+"F2.wireOp",EDGE,"E15.51.13.0")])],"isStart":true}),makeQuery(id+"F3.opExtrude","CAP_FACE",FACE,{"disambiguationData":[OSD([sQuery(id+"F2.wireOp",EDGE,"E15.3.14.0"),sQuery(id+"F2.wireOp",EDGE,"E15.10.14.0"),sQuery(id+"F2.wireOp",EDGE,"E15.14.14.0"),sQuery(id+"F2.wireOp",EDGE,"E15.18.14.0"),sQuery(id+"F2.wireOp",EDGE,"E15.22.14.0"),sQuery(id+"F2.wireOp",EDGE,"E15.26.14.0"),sQuery(id+"F2.wireOp",EDGE,"E15.30.14.0"),sQuery(id+"F2.wireOp",EDGE,"E15.33.14.0"),sQuery(id+"F2.wireOp",EDGE,"E15.37.14.0"),sQuery(id+"F2.wireOp",EDGE,"E15.41.14.0"),sQuery(id+"F2.wireOp",EDGE,"E15.44.14.0"),sQuery(id+"F2.wireOp",EDGE,"E15.48.14.0"),sQuery(id+"F2.wireOp",EDGE,"E15.51.14.0")])],"isStart":true}),makeQuery(id+"F3.opExtrude","CAP_FACE",FACE,{"disambiguationData":[OSD([sQuery(id+"F2.wireOp",EDGE,"E15.3.15.0"),sQuery(id+"F2.wireOp",EDGE,"E15.10.15.0"),sQuery(id+"F2.wireOp",EDGE,"E15.14.15.0"),sQuery(id+"F2.wireOp",EDGE,"E15.18.15.0"),sQuery(id+"F2.wireOp",EDGE,"E15.22.15.0"),sQuery(id+"F2.wireOp",EDGE,"E15.26.15.0"),sQuery(id+"F2.wireOp",EDGE,"E15.30.15.0"),sQuery(id+"F2.wireOp",EDGE,"E15.33.15.0"),sQuery(id+"F2.wireOp",EDGE,"E15.37.15.0"),sQuery(id+"F2.wireOp",EDGE,"E15.41.15.0"),sQuery(id+"F2.wireOp",EDGE,"E15.44.15.0"),sQuery(id+"F2.wireOp",EDGE,"E15.48.15.0"),sQuery(id+"F2.wireOp",EDGE,"E15.51.15.0")])],"isStart":true}),makeQuery(id+"F3.opExtrude","CAP_FACE",FACE,{"disambiguationData":[OSD([sQuery(id+"F2.wireOp",EDGE,"E15.3.16.0"),sQuery(id+"F2.wireOp",EDGE,"E15.10.16.0"),sQuery(id+"F2.wireOp",EDGE,"E15.14.16.0"),sQuery(id+"F2.wireOp",EDGE,"E15.18.16.0"),sQuery(id+"F2.wireOp",EDGE,"E15.22.16.0"),sQuery(id+"F2.wireOp",EDGE,"E15.26.16.0"),sQuery(id+"F2.wireOp",EDGE,"E15.30.16.0"),sQuery(id+"F2.wireOp",EDGE,"E15.33.16.0"),sQuery(id+"F2.wireOp",EDGE,"E15.37.16.0"),sQuery(id+"F2.wireOp",EDGE,"E15.41.16.0"),sQuery(id+"F2.wireOp",EDGE,"E15.44.16.0"),sQuery(id+"F2.wireOp",EDGE,"E15.48.16.0"),sQuery(id+"F2.wireOp",EDGE,"E15.51.16.0")])],"isStart":true}),makeQuery(id+"F3.opExtrude","CAP_FACE",FACE,{"disambiguationData":[OSD([sQuery(id+"F2.wireOp",EDGE,"E15.3.17.0"),sQuery(id+"F2.wireOp",EDGE,"E15.10.17.0"),sQuery(id+"F2.wireOp",EDGE,"E15.14.17.0"),sQuery(id+"F2.wireOp",EDGE,"E15.18.17.0"),sQuery(id+"F2.wireOp",EDGE,"E15.22.17.0"),sQuery(id+"F2.wireOp",EDGE,"E15.26.17.0"),sQuery(id+"F2.wireOp",EDGE,"E15.30.17.0"),sQuery(id+"F2.wireOp",EDGE,"E15.33.17.0"),sQuery(id+"F2.wireOp",EDGE,"E15.37.17.0"),sQuery(id+"F2.wireOp",EDGE,"E15.41.17.0"),sQuery(id+"F2.wireOp",EDGE,"E15.44.17.0"),sQuery(id+"F2.wireOp",EDGE,"E15.48.17.0"),sQuery(id+"F2.wireOp",EDGE,"E15.51.17.0")])],"isStart":true}),makeQuery(id+"F3.opExtrude","CAP_FACE",FACE,{"disambiguationData":[OSD([sQuery(id+"F2.wireOp",EDGE,"E15.3.18.0"),sQuery(id+"F2.wireOp",EDGE,"E15.10.18.0"),sQuery(id+"F2.wireOp",EDGE,"E15.14.18.0"),sQuery(id+"F2.wireOp",EDGE,"E15.18.18.0"),sQuery(id+"F2.wireOp",EDGE,"E15.22.18.0"),sQuery(id+"F2.wireOp",EDGE,"E15.26.18.0"),sQuery(id+"F2.wireOp",EDGE,"E15.30.18.0"),sQuery(id+"F2.wireOp",EDGE,"E15.33.18.0"),sQuery(id+"F2.wireOp",EDGE,"E15.37.18.0"),sQuery(id+"F2.wireOp",EDGE,"E15.41.18.0"),sQuery(id+"F2.wireOp",EDGE,"E15.44.18.0"),sQuery(id+"F2.wireOp",EDGE,"E15.48.18.0"),sQuery(id+"F2.wireOp",EDGE,"E15.51.18.0")])],"isStart":true}),makeQuery(id+"F3.opExtrude","CAP_FACE",FACE,{"disambiguationData":[OSD([sQuery(id+"F2.wireOp",EDGE,"E15.3.19.0"),sQuery(id+"F2.wireOp",EDGE,"E15.10.19.0"),sQuery(id+"F2.wireOp",EDGE,"E15.14.19.0"),sQuery(id+"F2.wireOp",EDGE,"E15.18.19.0"),sQuery(id+"F2.wireOp",EDGE,"E15.22.19.0"),sQuery(id+"F2.wireOp",EDGE,"E15.26.19.0"),sQuery(id+"F2.wireOp",EDGE,"E15.30.19.0"),sQuery(id+"F2.wireOp",EDGE,"E15.33.19.0"),sQuery(id+"F2.wireOp",EDGE,"E15.37.19.0"),sQuery(id+"F2.wireOp",EDGE,"E15.41.19.0"),sQuery(id+"F2.wireOp",EDGE,"E15.44.19.0"),sQuery(id+"F2.wireOp",EDGE,"E15.48.19.0"),sQuery(id+"F2.wireOp",EDGE,"E15.51.19.0")])],"isStart":true}),makeQuery(id+"F3.opExtrude","CAP_FACE",FACE,{"disambiguationData":[OSD([sQuery(id+"F2.wireOp",EDGE,"E15.3.20.0"),sQuery(id+"F2.wireOp",EDGE,"E15.10.20.0"),sQuery(id+"F2.wireOp",EDGE,"E15.14.20.0"),sQuery(id+"F2.wireOp",EDGE,"E15.18.20.0"),sQuery(id+"F2.wireOp",EDGE,"E15.22.20.0"),sQuery(id+"F2.wireOp",EDGE,"E15.26.20.0"),sQuery(id+"F2.wireOp",EDGE,"E15.30.20.0"),sQuery(id+"F2.wireOp",EDGE,"E15.33.20.0"),sQuery(id+"F2.wireOp",EDGE,"E15.37.20.0"),sQuery(id+"F2.wireOp",EDGE,"E15.41.20.0"),sQuery(id+"F2.wireOp",EDGE,"E15.44.20.0"),sQuery(id+"F2.wireOp",EDGE,"E15.48.20.0"),sQuery(id+"F2.wireOp",EDGE,"E15.51.20.0")])],"isStart":true}),makeQuery(id+"F3.opExtrude","CAP_FACE",FACE,{"disambiguationData":[OSD([sQuery(id+"F2.wireOp",EDGE,"E15.3.21.0"),sQuery(id+"F2.wireOp",EDGE,"E15.10.21.0"),sQuery(id+"F2.wireOp",EDGE,"E15.14.21.0"),sQuery(id+"F2.wireOp",EDGE,"E15.18.21.0"),sQuery(id+"F2.wireOp",EDGE,"E15.22.21.0"),sQuery(id+"F2.wireOp",EDGE,"E15.26.21.0"),sQuery(id+"F2.wireOp",EDGE,"E15.30.21.0"),sQuery(id+"F2.wireOp",EDGE,"E15.33.21.0"),sQuery(id+"F2.wireOp",EDGE,"E15.37.21.0"),sQuery(id+"F2.wireOp",EDGE,"E15.41.21.0"),sQuery(id+"F2.wireOp",EDGE,"E15.44.21.0"),sQuery(id+"F2.wireOp",EDGE,"E15.48.21.0"),sQuery(id+"F2.wireOp",EDGE,"E15.51.21.0")])],"isStart":true}),makeQuery(id+"F3.opExtrude","CAP_FACE",FACE,{"disambiguationData":[OSD([sQuery(id+"F2.wireOp",EDGE,"E15.3.22.0"),sQuery(id+"F2.wireOp",EDGE,"E15.10.22.0"),sQuery(id+"F2.wireOp",EDGE,"E15.14.22.0"),sQuery(id+"F2.wireOp",EDGE,"E15.18.22.0"),sQuery(id+"F2.wireOp",EDGE,"E15.22.22.0"),sQuery(id+"F2.wireOp",EDGE,"E15.26.22.0"),sQuery(id+"F2.wireOp",EDGE,"E15.30.22.0"),sQuery(id+"F2.wireOp",EDGE,"E15.33.22.0"),sQuery(id+"F2.wireOp",EDGE,"E15.37.22.0"),sQuery(id+"F2.wireOp",EDGE,"E15.41.22.0"),sQuery(id+"F2.wireOp",EDGE,"E15.44.22.0"),sQuery(id+"F2.wireOp",EDGE,"E15.48.22.0"),sQuery(id+"F2.wireOp",EDGE,"E15.51.22.0")])],"isStart":true}),makeQuery(id+"F3.opExtrude","CAP_FACE",FACE,{"disambiguationData":[OSD([sQuery(id+"F2.wireOp",EDGE,"E15.3.23.0"),sQuery(id+"F2.wireOp",EDGE,"E15.10.23.0"),sQuery(id+"F2.wireOp",EDGE,"E15.14.23.0"),sQuery(id+"F2.wireOp",EDGE,"E15.18.23.0"),sQuery(id+"F2.wireOp",EDGE,"E15.22.23.0"),sQuery(id+"F2.wireOp",EDGE,"E15.26.23.0"),sQuery(id+"F2.wireOp",EDGE,"E15.30.23.0"),sQuery(id+"F2.wireOp",EDGE,"E15.33.23.0"),sQuery(id+"F2.wireOp",EDGE,"E15.37.23.0"),sQuery(id+"F2.wireOp",EDGE,"E15.41.23.0"),sQuery(id+"F2.wireOp",EDGE,"E15.44.23.0"),sQuery(id+"F2.wireOp",EDGE,"E15.48.23.0"),sQuery(id+"F2.wireOp",EDGE,"E15.51.23.0")])],"isStart":true}),makeQuery(id+"F3.opExtrude","CAP_FACE",FACE,{"disambiguationData":[OSD([sQuery(id+"F2.wireOp",EDGE,"E15.3.24.0"),sQuery(id+"F2.wireOp",EDGE,"E15.10.24.0"),sQuery(id+"F2.wireOp",EDGE,"E15.14.24.0"),sQuery(id+"F2.wireOp",EDGE,"E15.18.24.0"),sQuery(id+"F2.wireOp",EDGE,"E15.22.24.0"),sQuery(id+"F2.wireOp",EDGE,"E15.26.24.0"),sQuery(id+"F2.wireOp",EDGE,"E15.30.24.0"),sQuery(id+"F2.wireOp",EDGE,"E15.33.24.0"),sQuery(id+"F2.wireOp",EDGE,"E15.37.24.0"),sQuery(id+"F2.wireOp",EDGE,"E15.41.24.0"),sQuery(id+"F2.wireOp",EDGE,"E15.44.24.0"),sQuery(id+"F2.wireOp",EDGE,"E15.48.24.0"),sQuery(id+"F2.wireOp",EDGE,"E15.51.24.0")])],"isStart":true}),makeQuery(id+"F3.opExtrude","CAP_FACE",FACE,{"disambiguationData":[OSD([sQuery(id+"F2.wireOp",EDGE,"E15.3.25.0"),sQuery(id+"F2.wireOp",EDGE,"E15.10.25.0"),sQuery(id+"F2.wireOp",EDGE,"E15.14.25.0"),sQuery(id+"F2.wireOp",EDGE,"E15.18.25.0"),sQuery(id+"F2.wireOp",EDGE,"E15.22.25.0"),sQuery(id+"F2.wireOp",EDGE,"E15.26.25.0"),sQuery(id+"F2.wireOp",EDGE,"E15.30.25.0"),sQuery(id+"F2.wireOp",EDGE,"E15.33.25.0"),sQuery(id+"F2.wireOp",EDGE,"E15.37.25.0"),sQuery(id+"F2.wireOp",EDGE,"E15.41.25.0"),sQuery(id+"F2.wireOp",EDGE,"E15.44.25.0"),sQuery(id+"F2.wireOp",EDGE,"E15.48.25.0"),sQuery(id+"F2.wireOp",EDGE,"E15.51.25.0")])],"isStart":true}),makeQuery(id+"F3.opExtrude","CAP_FACE",FACE,{"disambiguationData":[OSD([sQuery(id+"F2.wireOp",EDGE,"E15.3.26.0"),sQuery(id+"F2.wireOp",EDGE,"E15.10.26.0"),sQuery(id+"F2.wireOp",EDGE,"E15.14.26.0"),sQuery(id+"F2.wireOp",EDGE,"E15.18.26.0"),sQuery(id+"F2.wireOp",EDGE,"E15.22.26.0"),sQuery(id+"F2.wireOp",EDGE,"E15.26.26.0"),sQuery(id+"F2.wireOp",EDGE,"E15.30.26.0"),sQuery(id+"F2.wireOp",EDGE,"E15.33.26.0"),sQuery(id+"F2.wireOp",EDGE,"E15.37.26.0"),sQuery(id+"F2.wireOp",EDGE,"E15.41.26.0"),sQuery(id+"F2.wireOp",EDGE,"E15.44.26.0"),sQuery(id+"F2.wireOp",EDGE,"E15.48.26.0"),sQuery(id+"F2.wireOp",EDGE,"E15.51.26.0")])],"isStart":true}),makeQuery(id+"F3.opExtrude","CAP_FACE",FACE,{"disambiguationData":[OSD([sQuery(id+"F2.wireOp",EDGE,"E15.3.27.0"),sQuery(id+"F2.wireOp",EDGE,"E15.10.27.0"),sQuery(id+"F2.wireOp",EDGE,"E15.14.27.0"),sQuery(id+"F2.wireOp",EDGE,"E15.18.27.0"),sQuery(id+"F2.wireOp",EDGE,"E15.22.27.0"),sQuery(id+"F2.wireOp",EDGE,"E15.26.27.0"),sQuery(id+"F2.wireOp",EDGE,"E15.30.27.0"),sQuery(id+"F2.wireOp",EDGE,"E15.33.27.0"),sQuery(id+"F2.wireOp",EDGE,"E15.37.27.0"),sQuery(id+"F2.wireOp",EDGE,"E15.41.27.0"),sQuery(id+"F2.wireOp",EDGE,"E15.44.27.0"),sQuery(id+"F2.wireOp",EDGE,"E15.48.27.0"),sQuery(id+"F2.wireOp",EDGE,"E15.51.27.0")])],"isStart":true}),makeQuery(id+"F3.opExtrude","CAP_FACE",FACE,{"disambiguationData":[OSD([sQuery(id+"F2.wireOp",EDGE,"E15.3.28.0"),sQuery(id+"F2.wireOp",EDGE,"E15.10.28.0"),sQuery(id+"F2.wireOp",EDGE,"E15.14.28.0"),sQuery(id+"F2.wireOp",EDGE,"E15.18.28.0"),sQuery(id+"F2.wireOp",EDGE,"E15.22.28.0"),sQuery(id+"F2.wireOp",EDGE,"E15.26.28.0"),sQuery(id+"F2.wireOp",EDGE,"E15.30.28.0"),sQuery(id+"F2.wireOp",EDGE,"E15.33.28.0"),sQuery(id+"F2.wireOp",EDGE,"E15.37.28.0"),sQuery(id+"F2.wireOp",EDGE,"E15.41.28.0"),sQuery(id+"F2.wireOp",EDGE,"E15.44.28.0"),sQuery(id+"F2.wireOp",EDGE,"E15.48.28.0"),sQuery(id+"F2.wireOp",EDGE,"E15.51.28.0")])],"isStart":true}),makeQuery(id+"F3.opExtrude","CAP_FACE",FACE,{"disambiguationData":[OSD([sQuery(id+"F2.wireOp",EDGE,"E15.3.29.0"),sQuery(id+"F2.wireOp",EDGE,"E15.10.29.0"),sQuery(id+"F2.wireOp",EDGE,"E15.14.29.0"),sQuery(id+"F2.wireOp",EDGE,"E15.18.29.0"),sQuery(id+"F2.wireOp",EDGE,"E15.22.29.0"),sQuery(id+"F2.wireOp",EDGE,"E15.26.29.0"),sQuery(id+"F2.wireOp",EDGE,"E15.30.29.0"),sQuery(id+"F2.wireOp",EDGE,"E15.33.29.0"),sQuery(id+"F2.wireOp",EDGE,"E15.37.29.0"),sQuery(id+"F2.wireOp",EDGE,"E15.41.29.0"),sQuery(id+"F2.wireOp",EDGE,"E15.44.29.0"),sQuery(id+"F2.wireOp",EDGE,"E15.48.29.0"),sQuery(id+"F2.wireOp",EDGE,"E15.51.29.0")])],"isStart":true})]});
            var sketch = newSketch(context, id + "F4", { "sketchPlane" : qUnion([Q0])});
            skCircle(sketch, "E16", {"center": v(0, 0) * mm, "radius": 12.7 * mm});
            skSolve(sketch);
        }
        {
            var Q0;
            Q0=makeQuery(id+"F4.imprint","IMPRINT",FACE,{"disambiguationData":[TD([[makeQuery(id+"F4.imprint","IMPRINT",EDGE,{"derivedFrom":sQuery(id+"F4.wireOp",EDGE,"E16")}),1.0]])]});
            extrude(context, id + "F5", {"entities" : qUnion([Q0]), "operationType" : NewBodyOperationType.ADD, "depth" : 12.7 * mm});
        }
        {
            var Q0;
            Q0=makeQuery(id+"F5.opExtrude","CAP_FACE",FACE,{"disambiguationData":[OSD([sQuery(id+"F4.wireOp",EDGE,"E16")])],"isStart":false});
            var sketch = newSketch(context, id + "F6", { "sketchPlane" : qUnion([Q0])});
            skCircle(sketch, "E17", {"center": v(0, 0) * mm, "radius": 6.35 * mm});
            skSolve(sketch);
        }
        {
            var Q0;
            Q0 = qSketchRegion(id + "F6", true);
            extrude(context, id + "F7", {"entities" : qUnion([Q0]), "operationType" : NewBodyOperationType.REMOVE, "oppositeDirection" : true, "depth" : 127 * mm});
        }
        {
            var Q0;
            Q0=makeQuery(id+"F3.boolean.opBoolean","MERGE",FACE,{"derivedFrom":[makeQuery(id+"F1.opExtrude","CAP_FACE",FACE,{"disambiguationData":[OSD([sQuery(id+"F0.wireOp",EDGE,"E0")])],"isStart":true}),makeQuery(id+"F3.opExtrude","CAP_FACE",FACE,{"disambiguationData":[OSD([sQuery(id+"F2.wireOp",EDGE,"E1.trimOffspring"),sQuery(id+"F2.wireOp",EDGE,"E2"),sQuery(id+"F2.wireOp",EDGE,"E3"),sQuery(id+"F2.wireOp",EDGE,"E4.MirrorCS"),sQuery(id+"F2.wireOp",EDGE,"E5.MirrorCS"),sQuery(id+"F2.wireOp",EDGE,"E6.MirrorCS"),sQuery(id+"F2.wireOp",EDGE,"E7.filletArc"),sQuery(id+"F2.wireOp",EDGE,"E8.filletArc"),sQuery(id+"F2.wireOp",EDGE,"E9.filletArc"),sQuery(id+"F2.wireOp",EDGE,"E10.filletArc"),sQuery(id+"F2.wireOp",EDGE,"E11.filletArc"),sQuery(id+"F2.wireOp",EDGE,"E12.filletArc"),sQuery(id+"F2.wireOp",EDGE,"E13")])],"isStart":false}),makeQuery(id+"F3.opExtrude","CAP_FACE",FACE,{"disambiguationData":[OSD([sQuery(id+"F2.wireOp",EDGE,"E14.1.3"),sQuery(id+"F2.wireOp",EDGE,"E14.1.7"),sQuery(id+"F2.wireOp",EDGE,"E14.1.8"),sQuery(id+"F2.wireOp",EDGE,"E14.1.9"),sQuery(id+"F2.wireOp",EDGE,"E14.1.10"),sQuery(id+"F2.wireOp",EDGE,"E14.1.11"),sQuery(id+"F2.wireOp",EDGE,"E14.1.12"),sQuery(id+"F2.wireOp",EDGE,"E14.1.13"),sQuery(id+"F2.wireOp",EDGE,"E14.1.14"),sQuery(id+"F2.wireOp",EDGE,"E14.1.15"),sQuery(id+"F2.wireOp",EDGE,"E14.1.16"),sQuery(id+"F2.wireOp",EDGE,"E14.1.17"),sQuery(id+"F2.wireOp",EDGE,"E14.1.18")])],"isStart":false}),makeQuery(id+"F3.opExtrude","CAP_FACE",FACE,{"disambiguationData":[OSD([sQuery(id+"F2.wireOp",EDGE,"E14.2.3"),sQuery(id+"F2.wireOp",EDGE,"E14.2.7"),sQuery(id+"F2.wireOp",EDGE,"E14.2.8"),sQuery(id+"F2.wireOp",EDGE,"E14.2.9"),sQuery(id+"F2.wireOp",EDGE,"E14.2.10"),sQuery(id+"F2.wireOp",EDGE,"E14.2.11"),sQuery(id+"F2.wireOp",EDGE,"E14.2.12"),sQuery(id+"F2.wireOp",EDGE,"E14.2.13"),sQuery(id+"F2.wireOp",EDGE,"E14.2.14"),sQuery(id+"F2.wireOp",EDGE,"E14.2.15"),sQuery(id+"F2.wireOp",EDGE,"E14.2.16"),sQuery(id+"F2.wireOp",EDGE,"E14.2.17"),sQuery(id+"F2.wireOp",EDGE,"E14.2.18")])],"isStart":false}),makeQuery(id+"F3.opExtrude","CAP_FACE",FACE,{"disambiguationData":[OSD([sQuery(id+"F2.wireOp",EDGE,"E15.3.3.0"),sQuery(id+"F2.wireOp",EDGE,"E15.10.3.0"),sQuery(id+"F2.wireOp",EDGE,"E15.14.3.0"),sQuery(id+"F2.wireOp",EDGE,"E15.18.3.0"),sQuery(id+"F2.wireOp",EDGE,"E15.22.3.0"),sQuery(id+"F2.wireOp",EDGE,"E15.26.3.0"),sQuery(id+"F2.wireOp",EDGE,"E15.30.3.0"),sQuery(id+"F2.wireOp",EDGE,"E15.33.3.0"),sQuery(id+"F2.wireOp",EDGE,"E15.37.3.0"),sQuery(id+"F2.wireOp",EDGE,"E15.41.3.0"),sQuery(id+"F2.wireOp",EDGE,"E15.44.3.0"),sQuery(id+"F2.wireOp",EDGE,"E15.48.3.0"),sQuery(id+"F2.wireOp",EDGE,"E15.51.3.0")])],"isStart":false}),makeQuery(id+"F3.opExtrude","CAP_FACE",FACE,{"disambiguationData":[OSD([sQuery(id+"F2.wireOp",EDGE,"E15.3.4.0"),sQuery(id+"F2.wireOp",EDGE,"E15.10.4.0"),sQuery(id+"F2.wireOp",EDGE,"E15.14.4.0"),sQuery(id+"F2.wireOp",EDGE,"E15.18.4.0"),sQuery(id+"F2.wireOp",EDGE,"E15.22.4.0"),sQuery(id+"F2.wireOp",EDGE,"E15.26.4.0"),sQuery(id+"F2.wireOp",EDGE,"E15.30.4.0"),sQuery(id+"F2.wireOp",EDGE,"E15.33.4.0"),sQuery(id+"F2.wireOp",EDGE,"E15.37.4.0"),sQuery(id+"F2.wireOp",EDGE,"E15.41.4.0"),sQuery(id+"F2.wireOp",EDGE,"E15.44.4.0"),sQuery(id+"F2.wireOp",EDGE,"E15.48.4.0"),sQuery(id+"F2.wireOp",EDGE,"E15.51.4.0")])],"isStart":false}),makeQuery(id+"F3.opExtrude","CAP_FACE",FACE,{"disambiguationData":[OSD([sQuery(id+"F2.wireOp",EDGE,"E15.3.5.0"),sQuery(id+"F2.wireOp",EDGE,"E15.10.5.0"),sQuery(id+"F2.wireOp",EDGE,"E15.14.5.0"),sQuery(id+"F2.wireOp",EDGE,"E15.18.5.0"),sQuery(id+"F2.wireOp",EDGE,"E15.22.5.0"),sQuery(id+"F2.wireOp",EDGE,"E15.26.5.0"),sQuery(id+"F2.wireOp",EDGE,"E15.30.5.0"),sQuery(id+"F2.wireOp",EDGE,"E15.33.5.0"),sQuery(id+"F2.wireOp",EDGE,"E15.37.5.0"),sQuery(id+"F2.wireOp",EDGE,"E15.41.5.0"),sQuery(id+"F2.wireOp",EDGE,"E15.44.5.0"),sQuery(id+"F2.wireOp",EDGE,"E15.48.5.0"),sQuery(id+"F2.wireOp",EDGE,"E15.51.5.0")])],"isStart":false}),makeQuery(id+"F3.opExtrude","CAP_FACE",FACE,{"disambiguationData":[OSD([sQuery(id+"F2.wireOp",EDGE,"E15.3.6.0"),sQuery(id+"F2.wireOp",EDGE,"E15.10.6.0"),sQuery(id+"F2.wireOp",EDGE,"E15.14.6.0"),sQuery(id+"F2.wireOp",EDGE,"E15.18.6.0"),sQuery(id+"F2.wireOp",EDGE,"E15.22.6.0"),sQuery(id+"F2.wireOp",EDGE,"E15.26.6.0"),sQuery(id+"F2.wireOp",EDGE,"E15.30.6.0"),sQuery(id+"F2.wireOp",EDGE,"E15.33.6.0"),sQuery(id+"F2.wireOp",EDGE,"E15.37.6.0"),sQuery(id+"F2.wireOp",EDGE,"E15.41.6.0"),sQuery(id+"F2.wireOp",EDGE,"E15.44.6.0"),sQuery(id+"F2.wireOp",EDGE,"E15.48.6.0"),sQuery(id+"F2.wireOp",EDGE,"E15.51.6.0")])],"isStart":false}),makeQuery(id+"F3.opExtrude","CAP_FACE",FACE,{"disambiguationData":[OSD([sQuery(id+"F2.wireOp",EDGE,"E15.3.7.0"),sQuery(id+"F2.wireOp",EDGE,"E15.10.7.0"),sQuery(id+"F2.wireOp",EDGE,"E15.14.7.0"),sQuery(id+"F2.wireOp",EDGE,"E15.18.7.0"),sQuery(id+"F2.wireOp",EDGE,"E15.22.7.0"),sQuery(id+"F2.wireOp",EDGE,"E15.26.7.0"),sQuery(id+"F2.wireOp",EDGE,"E15.30.7.0"),sQuery(id+"F2.wireOp",EDGE,"E15.33.7.0"),sQuery(id+"F2.wireOp",EDGE,"E15.37.7.0"),sQuery(id+"F2.wireOp",EDGE,"E15.41.7.0"),sQuery(id+"F2.wireOp",EDGE,"E15.44.7.0"),sQuery(id+"F2.wireOp",EDGE,"E15.48.7.0"),sQuery(id+"F2.wireOp",EDGE,"E15.51.7.0")])],"isStart":false}),makeQuery(id+"F3.opExtrude","CAP_FACE",FACE,{"disambiguationData":[OSD([sQuery(id+"F2.wireOp",EDGE,"E15.3.8.0"),sQuery(id+"F2.wireOp",EDGE,"E15.10.8.0"),sQuery(id+"F2.wireOp",EDGE,"E15.14.8.0"),sQuery(id+"F2.wireOp",EDGE,"E15.18.8.0"),sQuery(id+"F2.wireOp",EDGE,"E15.22.8.0"),sQuery(id+"F2.wireOp",EDGE,"E15.26.8.0"),sQuery(id+"F2.wireOp",EDGE,"E15.30.8.0"),sQuery(id+"F2.wireOp",EDGE,"E15.33.8.0"),sQuery(id+"F2.wireOp",EDGE,"E15.37.8.0"),sQuery(id+"F2.wireOp",EDGE,"E15.41.8.0"),sQuery(id+"F2.wireOp",EDGE,"E15.44.8.0"),sQuery(id+"F2.wireOp",EDGE,"E15.48.8.0"),sQuery(id+"F2.wireOp",EDGE,"E15.51.8.0")])],"isStart":false}),makeQuery(id+"F3.opExtrude","CAP_FACE",FACE,{"disambiguationData":[OSD([sQuery(id+"F2.wireOp",EDGE,"E15.3.9.0"),sQuery(id+"F2.wireOp",EDGE,"E15.10.9.0"),sQuery(id+"F2.wireOp",EDGE,"E15.14.9.0"),sQuery(id+"F2.wireOp",EDGE,"E15.18.9.0"),sQuery(id+"F2.wireOp",EDGE,"E15.22.9.0"),sQuery(id+"F2.wireOp",EDGE,"E15.26.9.0"),sQuery(id+"F2.wireOp",EDGE,"E15.30.9.0"),sQuery(id+"F2.wireOp",EDGE,"E15.33.9.0"),sQuery(id+"F2.wireOp",EDGE,"E15.37.9.0"),sQuery(id+"F2.wireOp",EDGE,"E15.41.9.0"),sQuery(id+"F2.wireOp",EDGE,"E15.44.9.0"),sQuery(id+"F2.wireOp",EDGE,"E15.48.9.0"),sQuery(id+"F2.wireOp",EDGE,"E15.51.9.0")])],"isStart":false}),makeQuery(id+"F3.opExtrude","CAP_FACE",FACE,{"disambiguationData":[OSD([sQuery(id+"F2.wireOp",EDGE,"E15.3.10.0"),sQuery(id+"F2.wireOp",EDGE,"E15.10.10.0"),sQuery(id+"F2.wireOp",EDGE,"E15.14.10.0"),sQuery(id+"F2.wireOp",EDGE,"E15.18.10.0"),sQuery(id+"F2.wireOp",EDGE,"E15.22.10.0"),sQuery(id+"F2.wireOp",EDGE,"E15.26.10.0"),sQuery(id+"F2.wireOp",EDGE,"E15.30.10.0"),sQuery(id+"F2.wireOp",EDGE,"E15.33.10.0"),sQuery(id+"F2.wireOp",EDGE,"E15.37.10.0"),sQuery(id+"F2.wireOp",EDGE,"E15.41.10.0"),sQuery(id+"F2.wireOp",EDGE,"E15.44.10.0"),sQuery(id+"F2.wireOp",EDGE,"E15.48.10.0"),sQuery(id+"F2.wireOp",EDGE,"E15.51.10.0")])],"isStart":false}),makeQuery(id+"F3.opExtrude","CAP_FACE",FACE,{"disambiguationData":[OSD([sQuery(id+"F2.wireOp",EDGE,"E15.3.11.0"),sQuery(id+"F2.wireOp",EDGE,"E15.10.11.0"),sQuery(id+"F2.wireOp",EDGE,"E15.14.11.0"),sQuery(id+"F2.wireOp",EDGE,"E15.18.11.0"),sQuery(id+"F2.wireOp",EDGE,"E15.22.11.0"),sQuery(id+"F2.wireOp",EDGE,"E15.26.11.0"),sQuery(id+"F2.wireOp",EDGE,"E15.30.11.0"),sQuery(id+"F2.wireOp",EDGE,"E15.33.11.0"),sQuery(id+"F2.wireOp",EDGE,"E15.37.11.0"),sQuery(id+"F2.wireOp",EDGE,"E15.41.11.0"),sQuery(id+"F2.wireOp",EDGE,"E15.44.11.0"),sQuery(id+"F2.wireOp",EDGE,"E15.48.11.0"),sQuery(id+"F2.wireOp",EDGE,"E15.51.11.0")])],"isStart":false}),makeQuery(id+"F3.opExtrude","CAP_FACE",FACE,{"disambiguationData":[OSD([sQuery(id+"F2.wireOp",EDGE,"E15.3.12.0"),sQuery(id+"F2.wireOp",EDGE,"E15.10.12.0"),sQuery(id+"F2.wireOp",EDGE,"E15.14.12.0"),sQuery(id+"F2.wireOp",EDGE,"E15.18.12.0"),sQuery(id+"F2.wireOp",EDGE,"E15.22.12.0"),sQuery(id+"F2.wireOp",EDGE,"E15.26.12.0"),sQuery(id+"F2.wireOp",EDGE,"E15.30.12.0"),sQuery(id+"F2.wireOp",EDGE,"E15.33.12.0"),sQuery(id+"F2.wireOp",EDGE,"E15.37.12.0"),sQuery(id+"F2.wireOp",EDGE,"E15.41.12.0"),sQuery(id+"F2.wireOp",EDGE,"E15.44.12.0"),sQuery(id+"F2.wireOp",EDGE,"E15.48.12.0"),sQuery(id+"F2.wireOp",EDGE,"E15.51.12.0")])],"isStart":false}),makeQuery(id+"F3.opExtrude","CAP_FACE",FACE,{"disambiguationData":[OSD([sQuery(id+"F2.wireOp",EDGE,"E15.3.13.0"),sQuery(id+"F2.wireOp",EDGE,"E15.10.13.0"),sQuery(id+"F2.wireOp",EDGE,"E15.14.13.0"),sQuery(id+"F2.wireOp",EDGE,"E15.18.13.0"),sQuery(id+"F2.wireOp",EDGE,"E15.22.13.0"),sQuery(id+"F2.wireOp",EDGE,"E15.26.13.0"),sQuery(id+"F2.wireOp",EDGE,"E15.30.13.0"),sQuery(id+"F2.wireOp",EDGE,"E15.33.13.0"),sQuery(id+"F2.wireOp",EDGE,"E15.37.13.0"),sQuery(id+"F2.wireOp",EDGE,"E15.41.13.0"),sQuery(id+"F2.wireOp",EDGE,"E15.44.13.0"),sQuery(id+"F2.wireOp",EDGE,"E15.48.13.0"),sQuery(id+"F2.wireOp",EDGE,"E15.51.13.0")])],"isStart":false}),makeQuery(id+"F3.opExtrude","CAP_FACE",FACE,{"disambiguationData":[OSD([sQuery(id+"F2.wireOp",EDGE,"E15.3.14.0"),sQuery(id+"F2.wireOp",EDGE,"E15.10.14.0"),sQuery(id+"F2.wireOp",EDGE,"E15.14.14.0"),sQuery(id+"F2.wireOp",EDGE,"E15.18.14.0"),sQuery(id+"F2.wireOp",EDGE,"E15.22.14.0"),sQuery(id+"F2.wireOp",EDGE,"E15.26.14.0"),sQuery(id+"F2.wireOp",EDGE,"E15.30.14.0"),sQuery(id+"F2.wireOp",EDGE,"E15.33.14.0"),sQuery(id+"F2.wireOp",EDGE,"E15.37.14.0"),sQuery(id+"F2.wireOp",EDGE,"E15.41.14.0"),sQuery(id+"F2.wireOp",EDGE,"E15.44.14.0"),sQuery(id+"F2.wireOp",EDGE,"E15.48.14.0"),sQuery(id+"F2.wireOp",EDGE,"E15.51.14.0")])],"isStart":false}),makeQuery(id+"F3.opExtrude","CAP_FACE",FACE,{"disambiguationData":[OSD([sQuery(id+"F2.wireOp",EDGE,"E15.3.15.0"),sQuery(id+"F2.wireOp",EDGE,"E15.10.15.0"),sQuery(id+"F2.wireOp",EDGE,"E15.14.15.0"),sQuery(id+"F2.wireOp",EDGE,"E15.18.15.0"),sQuery(id+"F2.wireOp",EDGE,"E15.22.15.0"),sQuery(id+"F2.wireOp",EDGE,"E15.26.15.0"),sQuery(id+"F2.wireOp",EDGE,"E15.30.15.0"),sQuery(id+"F2.wireOp",EDGE,"E15.33.15.0"),sQuery(id+"F2.wireOp",EDGE,"E15.37.15.0"),sQuery(id+"F2.wireOp",EDGE,"E15.41.15.0"),sQuery(id+"F2.wireOp",EDGE,"E15.44.15.0"),sQuery(id+"F2.wireOp",EDGE,"E15.48.15.0"),sQuery(id+"F2.wireOp",EDGE,"E15.51.15.0")])],"isStart":false}),makeQuery(id+"F3.opExtrude","CAP_FACE",FACE,{"disambiguationData":[OSD([sQuery(id+"F2.wireOp",EDGE,"E15.3.16.0"),sQuery(id+"F2.wireOp",EDGE,"E15.10.16.0"),sQuery(id+"F2.wireOp",EDGE,"E15.14.16.0"),sQuery(id+"F2.wireOp",EDGE,"E15.18.16.0"),sQuery(id+"F2.wireOp",EDGE,"E15.22.16.0"),sQuery(id+"F2.wireOp",EDGE,"E15.26.16.0"),sQuery(id+"F2.wireOp",EDGE,"E15.30.16.0"),sQuery(id+"F2.wireOp",EDGE,"E15.33.16.0"),sQuery(id+"F2.wireOp",EDGE,"E15.37.16.0"),sQuery(id+"F2.wireOp",EDGE,"E15.41.16.0"),sQuery(id+"F2.wireOp",EDGE,"E15.44.16.0"),sQuery(id+"F2.wireOp",EDGE,"E15.48.16.0"),sQuery(id+"F2.wireOp",EDGE,"E15.51.16.0")])],"isStart":false}),makeQuery(id+"F3.opExtrude","CAP_FACE",FACE,{"disambiguationData":[OSD([sQuery(id+"F2.wireOp",EDGE,"E15.3.17.0"),sQuery(id+"F2.wireOp",EDGE,"E15.10.17.0"),sQuery(id+"F2.wireOp",EDGE,"E15.14.17.0"),sQuery(id+"F2.wireOp",EDGE,"E15.18.17.0"),sQuery(id+"F2.wireOp",EDGE,"E15.22.17.0"),sQuery(id+"F2.wireOp",EDGE,"E15.26.17.0"),sQuery(id+"F2.wireOp",EDGE,"E15.30.17.0"),sQuery(id+"F2.wireOp",EDGE,"E15.33.17.0"),sQuery(id+"F2.wireOp",EDGE,"E15.37.17.0"),sQuery(id+"F2.wireOp",EDGE,"E15.41.17.0"),sQuery(id+"F2.wireOp",EDGE,"E15.44.17.0"),sQuery(id+"F2.wireOp",EDGE,"E15.48.17.0"),sQuery(id+"F2.wireOp",EDGE,"E15.51.17.0")])],"isStart":false}),makeQuery(id+"F3.opExtrude","CAP_FACE",FACE,{"disambiguationData":[OSD([sQuery(id+"F2.wireOp",EDGE,"E15.3.18.0"),sQuery(id+"F2.wireOp",EDGE,"E15.10.18.0"),sQuery(id+"F2.wireOp",EDGE,"E15.14.18.0"),sQuery(id+"F2.wireOp",EDGE,"E15.18.18.0"),sQuery(id+"F2.wireOp",EDGE,"E15.22.18.0"),sQuery(id+"F2.wireOp",EDGE,"E15.26.18.0"),sQuery(id+"F2.wireOp",EDGE,"E15.30.18.0"),sQuery(id+"F2.wireOp",EDGE,"E15.33.18.0"),sQuery(id+"F2.wireOp",EDGE,"E15.37.18.0"),sQuery(id+"F2.wireOp",EDGE,"E15.41.18.0"),sQuery(id+"F2.wireOp",EDGE,"E15.44.18.0"),sQuery(id+"F2.wireOp",EDGE,"E15.48.18.0"),sQuery(id+"F2.wireOp",EDGE,"E15.51.18.0")])],"isStart":false}),makeQuery(id+"F3.opExtrude","CAP_FACE",FACE,{"disambiguationData":[OSD([sQuery(id+"F2.wireOp",EDGE,"E15.3.19.0"),sQuery(id+"F2.wireOp",EDGE,"E15.10.19.0"),sQuery(id+"F2.wireOp",EDGE,"E15.14.19.0"),sQuery(id+"F2.wireOp",EDGE,"E15.18.19.0"),sQuery(id+"F2.wireOp",EDGE,"E15.22.19.0"),sQuery(id+"F2.wireOp",EDGE,"E15.26.19.0"),sQuery(id+"F2.wireOp",EDGE,"E15.30.19.0"),sQuery(id+"F2.wireOp",EDGE,"E15.33.19.0"),sQuery(id+"F2.wireOp",EDGE,"E15.37.19.0"),sQuery(id+"F2.wireOp",EDGE,"E15.41.19.0"),sQuery(id+"F2.wireOp",EDGE,"E15.44.19.0"),sQuery(id+"F2.wireOp",EDGE,"E15.48.19.0"),sQuery(id+"F2.wireOp",EDGE,"E15.51.19.0")])],"isStart":false}),makeQuery(id+"F3.opExtrude","CAP_FACE",FACE,{"disambiguationData":[OSD([sQuery(id+"F2.wireOp",EDGE,"E15.3.20.0"),sQuery(id+"F2.wireOp",EDGE,"E15.10.20.0"),sQuery(id+"F2.wireOp",EDGE,"E15.14.20.0"),sQuery(id+"F2.wireOp",EDGE,"E15.18.20.0"),sQuery(id+"F2.wireOp",EDGE,"E15.22.20.0"),sQuery(id+"F2.wireOp",EDGE,"E15.26.20.0"),sQuery(id+"F2.wireOp",EDGE,"E15.30.20.0"),sQuery(id+"F2.wireOp",EDGE,"E15.33.20.0"),sQuery(id+"F2.wireOp",EDGE,"E15.37.20.0"),sQuery(id+"F2.wireOp",EDGE,"E15.41.20.0"),sQuery(id+"F2.wireOp",EDGE,"E15.44.20.0"),sQuery(id+"F2.wireOp",EDGE,"E15.48.20.0"),sQuery(id+"F2.wireOp",EDGE,"E15.51.20.0")])],"isStart":false}),makeQuery(id+"F3.opExtrude","CAP_FACE",FACE,{"disambiguationData":[OSD([sQuery(id+"F2.wireOp",EDGE,"E15.3.21.0"),sQuery(id+"F2.wireOp",EDGE,"E15.10.21.0"),sQuery(id+"F2.wireOp",EDGE,"E15.14.21.0"),sQuery(id+"F2.wireOp",EDGE,"E15.18.21.0"),sQuery(id+"F2.wireOp",EDGE,"E15.22.21.0"),sQuery(id+"F2.wireOp",EDGE,"E15.26.21.0"),sQuery(id+"F2.wireOp",EDGE,"E15.30.21.0"),sQuery(id+"F2.wireOp",EDGE,"E15.33.21.0"),sQuery(id+"F2.wireOp",EDGE,"E15.37.21.0"),sQuery(id+"F2.wireOp",EDGE,"E15.41.21.0"),sQuery(id+"F2.wireOp",EDGE,"E15.44.21.0"),sQuery(id+"F2.wireOp",EDGE,"E15.48.21.0"),sQuery(id+"F2.wireOp",EDGE,"E15.51.21.0")])],"isStart":false}),makeQuery(id+"F3.opExtrude","CAP_FACE",FACE,{"disambiguationData":[OSD([sQuery(id+"F2.wireOp",EDGE,"E15.3.22.0"),sQuery(id+"F2.wireOp",EDGE,"E15.10.22.0"),sQuery(id+"F2.wireOp",EDGE,"E15.14.22.0"),sQuery(id+"F2.wireOp",EDGE,"E15.18.22.0"),sQuery(id+"F2.wireOp",EDGE,"E15.22.22.0"),sQuery(id+"F2.wireOp",EDGE,"E15.26.22.0"),sQuery(id+"F2.wireOp",EDGE,"E15.30.22.0"),sQuery(id+"F2.wireOp",EDGE,"E15.33.22.0"),sQuery(id+"F2.wireOp",EDGE,"E15.37.22.0"),sQuery(id+"F2.wireOp",EDGE,"E15.41.22.0"),sQuery(id+"F2.wireOp",EDGE,"E15.44.22.0"),sQuery(id+"F2.wireOp",EDGE,"E15.48.22.0"),sQuery(id+"F2.wireOp",EDGE,"E15.51.22.0")])],"isStart":false}),makeQuery(id+"F3.opExtrude","CAP_FACE",FACE,{"disambiguationData":[OSD([sQuery(id+"F2.wireOp",EDGE,"E15.3.23.0"),sQuery(id+"F2.wireOp",EDGE,"E15.10.23.0"),sQuery(id+"F2.wireOp",EDGE,"E15.14.23.0"),sQuery(id+"F2.wireOp",EDGE,"E15.18.23.0"),sQuery(id+"F2.wireOp",EDGE,"E15.22.23.0"),sQuery(id+"F2.wireOp",EDGE,"E15.26.23.0"),sQuery(id+"F2.wireOp",EDGE,"E15.30.23.0"),sQuery(id+"F2.wireOp",EDGE,"E15.33.23.0"),sQuery(id+"F2.wireOp",EDGE,"E15.37.23.0"),sQuery(id+"F2.wireOp",EDGE,"E15.41.23.0"),sQuery(id+"F2.wireOp",EDGE,"E15.44.23.0"),sQuery(id+"F2.wireOp",EDGE,"E15.48.23.0"),sQuery(id+"F2.wireOp",EDGE,"E15.51.23.0")])],"isStart":false}),makeQuery(id+"F3.opExtrude","CAP_FACE",FACE,{"disambiguationData":[OSD([sQuery(id+"F2.wireOp",EDGE,"E15.3.24.0"),sQuery(id+"F2.wireOp",EDGE,"E15.10.24.0"),sQuery(id+"F2.wireOp",EDGE,"E15.14.24.0"),sQuery(id+"F2.wireOp",EDGE,"E15.18.24.0"),sQuery(id+"F2.wireOp",EDGE,"E15.22.24.0"),sQuery(id+"F2.wireOp",EDGE,"E15.26.24.0"),sQuery(id+"F2.wireOp",EDGE,"E15.30.24.0"),sQuery(id+"F2.wireOp",EDGE,"E15.33.24.0"),sQuery(id+"F2.wireOp",EDGE,"E15.37.24.0"),sQuery(id+"F2.wireOp",EDGE,"E15.41.24.0"),sQuery(id+"F2.wireOp",EDGE,"E15.44.24.0"),sQuery(id+"F2.wireOp",EDGE,"E15.48.24.0"),sQuery(id+"F2.wireOp",EDGE,"E15.51.24.0")])],"isStart":false}),makeQuery(id+"F3.opExtrude","CAP_FACE",FACE,{"disambiguationData":[OSD([sQuery(id+"F2.wireOp",EDGE,"E15.3.25.0"),sQuery(id+"F2.wireOp",EDGE,"E15.10.25.0"),sQuery(id+"F2.wireOp",EDGE,"E15.14.25.0"),sQuery(id+"F2.wireOp",EDGE,"E15.18.25.0"),sQuery(id+"F2.wireOp",EDGE,"E15.22.25.0"),sQuery(id+"F2.wireOp",EDGE,"E15.26.25.0"),sQuery(id+"F2.wireOp",EDGE,"E15.30.25.0"),sQuery(id+"F2.wireOp",EDGE,"E15.33.25.0"),sQuery(id+"F2.wireOp",EDGE,"E15.37.25.0"),sQuery(id+"F2.wireOp",EDGE,"E15.41.25.0"),sQuery(id+"F2.wireOp",EDGE,"E15.44.25.0"),sQuery(id+"F2.wireOp",EDGE,"E15.48.25.0"),sQuery(id+"F2.wireOp",EDGE,"E15.51.25.0")])],"isStart":false}),makeQuery(id+"F3.opExtrude","CAP_FACE",FACE,{"disambiguationData":[OSD([sQuery(id+"F2.wireOp",EDGE,"E15.3.26.0"),sQuery(id+"F2.wireOp",EDGE,"E15.10.26.0"),sQuery(id+"F2.wireOp",EDGE,"E15.14.26.0"),sQuery(id+"F2.wireOp",EDGE,"E15.18.26.0"),sQuery(id+"F2.wireOp",EDGE,"E15.22.26.0"),sQuery(id+"F2.wireOp",EDGE,"E15.26.26.0"),sQuery(id+"F2.wireOp",EDGE,"E15.30.26.0"),sQuery(id+"F2.wireOp",EDGE,"E15.33.26.0"),sQuery(id+"F2.wireOp",EDGE,"E15.37.26.0"),sQuery(id+"F2.wireOp",EDGE,"E15.41.26.0"),sQuery(id+"F2.wireOp",EDGE,"E15.44.26.0"),sQuery(id+"F2.wireOp",EDGE,"E15.48.26.0"),sQuery(id+"F2.wireOp",EDGE,"E15.51.26.0")])],"isStart":false}),makeQuery(id+"F3.opExtrude","CAP_FACE",FACE,{"disambiguationData":[OSD([sQuery(id+"F2.wireOp",EDGE,"E15.3.27.0"),sQuery(id+"F2.wireOp",EDGE,"E15.10.27.0"),sQuery(id+"F2.wireOp",EDGE,"E15.14.27.0"),sQuery(id+"F2.wireOp",EDGE,"E15.18.27.0"),sQuery(id+"F2.wireOp",EDGE,"E15.22.27.0"),sQuery(id+"F2.wireOp",EDGE,"E15.26.27.0"),sQuery(id+"F2.wireOp",EDGE,"E15.30.27.0"),sQuery(id+"F2.wireOp",EDGE,"E15.33.27.0"),sQuery(id+"F2.wireOp",EDGE,"E15.37.27.0"),sQuery(id+"F2.wireOp",EDGE,"E15.41.27.0"),sQuery(id+"F2.wireOp",EDGE,"E15.44.27.0"),sQuery(id+"F2.wireOp",EDGE,"E15.48.27.0"),sQuery(id+"F2.wireOp",EDGE,"E15.51.27.0")])],"isStart":false}),makeQuery(id+"F3.opExtrude","CAP_FACE",FACE,{"disambiguationData":[OSD([sQuery(id+"F2.wireOp",EDGE,"E15.3.28.0"),sQuery(id+"F2.wireOp",EDGE,"E15.10.28.0"),sQuery(id+"F2.wireOp",EDGE,"E15.14.28.0"),sQuery(id+"F2.wireOp",EDGE,"E15.18.28.0"),sQuery(id+"F2.wireOp",EDGE,"E15.22.28.0"),sQuery(id+"F2.wireOp",EDGE,"E15.26.28.0"),sQuery(id+"F2.wireOp",EDGE,"E15.30.28.0"),sQuery(id+"F2.wireOp",EDGE,"E15.33.28.0"),sQuery(id+"F2.wireOp",EDGE,"E15.37.28.0"),sQuery(id+"F2.wireOp",EDGE,"E15.41.28.0"),sQuery(id+"F2.wireOp",EDGE,"E15.44.28.0"),sQuery(id+"F2.wireOp",EDGE,"E15.48.28.0"),sQuery(id+"F2.wireOp",EDGE,"E15.51.28.0")])],"isStart":false}),makeQuery(id+"F3.opExtrude","CAP_FACE",FACE,{"disambiguationData":[OSD([sQuery(id+"F2.wireOp",EDGE,"E15.3.29.0"),sQuery(id+"F2.wireOp",EDGE,"E15.10.29.0"),sQuery(id+"F2.wireOp",EDGE,"E15.14.29.0"),sQuery(id+"F2.wireOp",EDGE,"E15.18.29.0"),sQuery(id+"F2.wireOp",EDGE,"E15.22.29.0"),sQuery(id+"F2.wireOp",EDGE,"E15.26.29.0"),sQuery(id+"F2.wireOp",EDGE,"E15.30.29.0"),sQuery(id+"F2.wireOp",EDGE,"E15.33.29.0"),sQuery(id+"F2.wireOp",EDGE,"E15.37.29.0"),sQuery(id+"F2.wireOp",EDGE,"E15.41.29.0"),sQuery(id+"F2.wireOp",EDGE,"E15.44.29.0"),sQuery(id+"F2.wireOp",EDGE,"E15.48.29.0"),sQuery(id+"F2.wireOp",EDGE,"E15.51.29.0")])],"isStart":false})]});
            var sketch = newSketch(context, id + "F8", { "sketchPlane" : qUnion([Q0])});
            skText(sketch, "E18", { "text": "PHAN", "fontName": "RobotoSlab-Regular.ttf"});
            skText(sketch, "E19", { "text": "LIKES", "fontName": "Arimo-Italic.ttf"});
            skText(sketch, "E20", { "text": "BUTT", "fontName": "AllertaStencil-Regular.ttf"});
            const initialGuessF8  = {"E18": [-0.02033, 0.01659, 1, 0, 0.01033], "E19": [-0.0265, -0.00472, 1, 0, 0.01322], "E20": [-0.0184, -0.01962, 1, 0, 0.01201]};
            skSetInitialGuess(sketch, initialGuessF8);
            skSolve(sketch);
        }
        {
            var Q0;
            Q0 = qSketchRegion(id + "F8", true);
            extrude(context, id + "F9", {"entities" : qUnion([Q0]), "operationType" : NewBodyOperationType.REMOVE, "oppositeDirection" : true, "depth" : 381 * mm});
        }
    });
